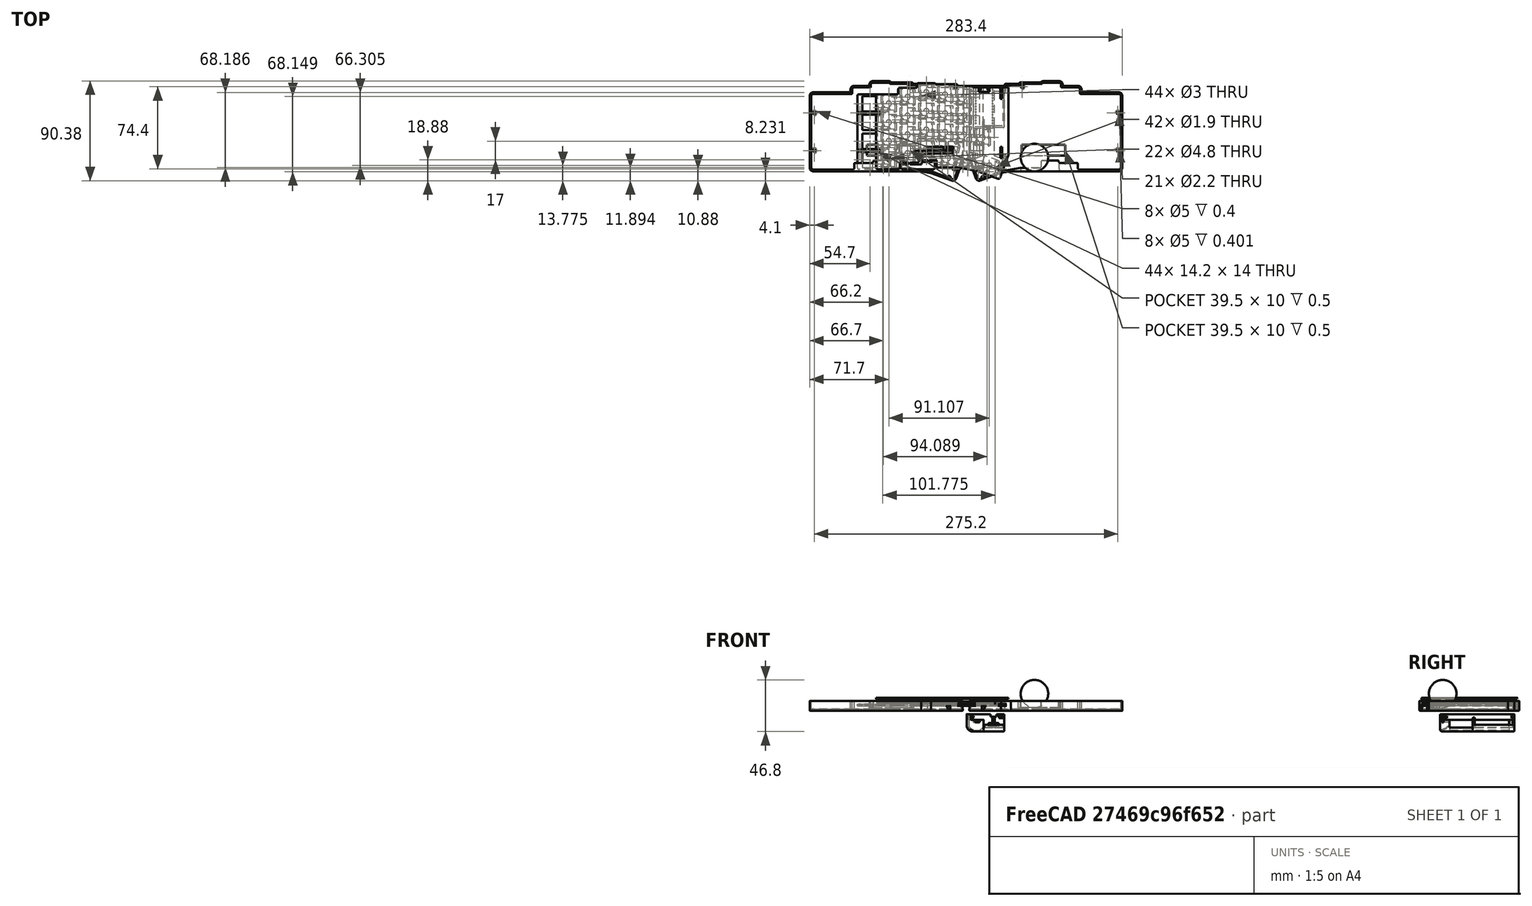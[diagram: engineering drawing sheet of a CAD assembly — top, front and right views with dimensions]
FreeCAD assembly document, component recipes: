
FREECAD ASSEMBLY — COMPONENT RECIPES ("simple-case-MS")

This assembly document has 5 components, labeled P0..P4 below (a component is one placed body or linked part). 4 of them carry a construction recipe — the FreeCAD feature program that regenerates the part from scratch, quoted from this document or its linked companion documents; the rest are supplied as boundary geometry only. No exploded tour is included for this assembly.
NOTE — document 2 of 3 of this assembly tour. The two overview renders and the header above are repeated from document 1; the component sections below continue where the previous document stopped.
COMPONENT P2 — recipe-attached ("case-key001", modeled in this document).
Construction recipe (the document's own serialized feature program — sketch geometry with constraints, then the solid features built on it; lengths are millimeters unless a unit is written):

FEATURE [Sketcher::SketchObject] Sketch020  label="top-plate"
  ArcFitTolerance = 1e-06
  ExternalTypes = [0]
  FullyConstrained = true
  MakeInternals = false
  Placement = pos=(0,0,6.6e-15) rot=(0,0,1;0rad)
  _ExternalGeoVersion = 0
  sketch-geometry (128):
    g0: ArcOfCircle CenterX=45.3 CenterY=2.4 CenterZ=0 NormalX=-1e-16 NormalY=0 NormalZ=1 AngleXU=1.5708 Radius=1.5 StartAngle=0 EndAngle=1.22777
    g1: LineSegment StartX=59.4 StartY=3.9 StartZ=0 EndX=45.3 EndY=3.9 EndZ=0
    g2: LineSegment StartX=43.8874 StartY=2.9045 StartZ=0 EndX=43.8874 EndY=2.8 EndZ=0
    g3: ArcOfCircle CenterX=59.4 CenterY=2.4 CenterZ=0 NormalX=-1e-16 NormalY=0 NormalZ=1 AngleXU=3.90995e-07 Radius=1.5 StartAngle=0 EndAngle=1.5708
    g4: LineSegment StartX=60.9 StartY=-0.4 StartZ=0 EndX=60.9 EndY=2.4 EndZ=0
    g5: LineSegment StartX=76.4 StartY=-0.4 StartZ=0 EndX=60.9 EndY=-0.4 EndZ=0
    g6: ArcOfCircle CenterX=76.4 CenterY=-1.9 CenterZ=0 NormalX=-1e-16 NormalY=0 NormalZ=1 AngleXU=3.90995e-07 Radius=1.5 StartAngle=0 EndAngle=1.5708
    g7: LineSegment StartX=77.9 StartY=-6.3 StartZ=0 EndX=77.9 EndY=-1.9 EndZ=0
    g8: LineSegment StartX=96.4 StartY=-6.3 StartZ=0 EndX=77.9 EndY=-6.3 EndZ=0
    g9: ArcOfCircle CenterX=96.4 CenterY=-7.8 CenterZ=0 NormalX=-1e-16 NormalY=0 NormalZ=1 AngleXU=3.90995e-07 Radius=1.5 StartAngle=0 EndAngle=1.5708
    g10: LineSegment StartX=97.9 StartY=-59.8 StartZ=0 EndX=97.9 EndY=-7.8 EndZ=0
    g11: LineSegment StartX=97.9 StartY=-72.8 StartZ=0 EndX=97.9 EndY=-59.8 EndZ=0
    g12: ArcOfCircle CenterX=96.4 CenterY=-72.8 CenterZ=0 NormalX=-1e-16 NormalY=0 NormalZ=1 AngleXU=-1.5708 Radius=1.5 StartAngle=0 EndAngle=1.5708
    g13: LineSegment StartX=78 StartY=-74.3 StartZ=0 EndX=96.4 EndY=-74.3 EndZ=0
    g14: ArcOfCircle CenterX=78 CenterY=-72.8 CenterZ=0 NormalX=-1e-16 NormalY=0 NormalZ=1 AngleXU=-3.14159 Radius=1.5 StartAngle=0 EndAngle=1.5708
    g15: LineSegment StartX=76.5 StartY=-68.4 StartZ=0 EndX=76.5 EndY=-72.8 EndZ=0
    g16: LineSegment StartX=60.7 StartY=-68.4 StartZ=0 EndX=76.5 EndY=-68.4 EndZ=0
    g17: ArcOfCircle CenterX=60.7 CenterY=-66.9 CenterZ=0 NormalX=-1e-16 NormalY=0 NormalZ=1 AngleXU=-3.14159 Radius=1.5 StartAngle=0 EndAngle=1.5708
    g18: LineSegment StartX=59.2 StartY=-66.1 StartZ=0 EndX=59.2 EndY=-66.9 EndZ=0
    g19: LineSegment StartX=43.1 StartY=-66.1 StartZ=0 EndX=59.2 EndY=-66.1 EndZ=0
    g20: LineSegment StartX=43.1 StartY=-71.2 StartZ=0 EndX=43.1 EndY=-66.1 EndZ=0
    g21: ArcOfCircle CenterX=41.6 CenterY=-71.2 CenterZ=0 NormalX=-1e-16 NormalY=0 NormalZ=1 AngleXU=-1.5708 Radius=1.5 StartAngle=0 EndAngle=1.5708
    g22: LineSegment StartX=41.4 StartY=-72.7 StartZ=0 EndX=41.6 EndY=-72.7 EndZ=0
    g23: LineSegment StartX=24.227 StartY=-72.7043 StartZ=0 EndX=41.4 EndY=-72.7 EndZ=0
    g24: LineSegment StartX=6.18739 StartY=-75.9853 StartZ=0 EndX=24.227 EndY=-72.7043 EndZ=0
    g25: LineSegment StartX=-12.4977 StartY=-82.7894 StartZ=0 EndX=6.18739 EndY=-75.9853 EndZ=0
    g26: ArcOfCircle CenterX=-13.0109 CenterY=-81.3798 CenterZ=0 NormalX=-1e-16 NormalY=0 NormalZ=1 AngleXU=-2.78723 Radius=1.50005 StartAngle=0 EndAngle=1.56562
    g27: LineSegment StartX=-20.3 StartY=-66 StartZ=0 EndX=-14.4178 EndY=-81.9004 EndZ=0
    g28: LineSegment StartX=-9.1 StartY=-61.9235 StartZ=0 EndX=-20.3 EndY=-66 EndZ=0
    g29: LineSegment StartX=-9.1 StartY=-61 StartZ=0 EndX=-9.1 EndY=-61.9235 EndZ=0
    g30: LineSegment StartX=-9.1 StartY=-36.9 StartZ=0 EndX=-9.1 EndY=-61 EndZ=0
    g31: LineSegment StartX=9.9 StartY=-36.9 StartZ=0 EndX=-9.1 EndY=-36.9 EndZ=0
    g32: LineSegment StartX=9.9 StartY=1.3 StartZ=0 EndX=9.9 EndY=-36.9 EndZ=0
    g33: LineSegment StartX=23.7 StartY=1.3 StartZ=0 EndX=9.9 EndY=1.3 EndZ=0
    g34: ArcOfCircle CenterX=25.2 CenterY=1.3 CenterZ=0 NormalX=-1e-16 NormalY=0 NormalZ=1 AngleXU=1.5708 Radius=1.5 StartAngle=0 EndAngle=1.5708
    g35: LineSegment StartX=43.8874 StartY=2.8 StartZ=0 EndX=25.2 EndY=2.8 EndZ=0
    g36: LineSegment StartX=93.5 StartY=-72.8 StartZ=0 EndX=79.3 EndY=-72.8 EndZ=0
    g37: LineSegment StartX=93.5 StartY=-58.8 StartZ=0 EndX=93.5 EndY=-72.8 EndZ=0
    g38: LineSegment StartX=79.3 StartY=-58.8 StartZ=0 EndX=93.5 EndY=-58.8 EndZ=0
    g39: LineSegment StartX=79.3 StartY=-72.8 StartZ=0 EndX=79.3 EndY=-58.8 EndZ=0
    g40: LineSegment StartX=76.5 StartY=-66.85 StartZ=0 EndX=62.3 EndY=-66.85 EndZ=0
    g41: LineSegment StartX=76.5 StartY=-52.85 StartZ=0 EndX=76.5 EndY=-66.85 EndZ=0
    g42: LineSegment StartX=62.3 StartY=-52.85 StartZ=0 EndX=76.5 EndY=-52.85 EndZ=0
    g43: LineSegment StartX=62.3 StartY=-66.85 StartZ=0 EndX=62.3 EndY=-52.85 EndZ=0
    g44: Circle CenterX=95.6 CenterY=-57.3 CenterZ=0 NormalX=-1e-16 NormalY=0 NormalZ=1 AngleXU=-1.5708 Radius=1.1
    g45: LineSegment StartX=93.5 StartY=-55.8 StartZ=0 EndX=79.3 EndY=-55.8 EndZ=0
    g46: LineSegment StartX=93.5 StartY=-41.8 StartZ=0 EndX=93.5 EndY=-55.8 EndZ=0
    g47: LineSegment StartX=79.3 StartY=-41.8 StartZ=0 EndX=93.5 EndY=-41.8 EndZ=0
    g48: LineSegment StartX=79.3 StartY=-55.8 StartZ=0 EndX=79.3 EndY=-41.8 EndZ=0
    g49: LineSegment StartX=76.5 StartY=-49.85 StartZ=0 EndX=62.3 EndY=-49.85 EndZ=0
    g50: LineSegment StartX=76.5 StartY=-35.85 StartZ=0 EndX=76.5 EndY=-49.85 EndZ=0
    g51: LineSegment StartX=62.3 StartY=-35.85 StartZ=0 EndX=76.5 EndY=-35.85 EndZ=0
    g52: LineSegment StartX=62.3 StartY=-49.85 StartZ=0 EndX=62.3 EndY=-35.85 EndZ=0
    g53: LineSegment StartX=59.5 StartY=-62.6 StartZ=0 EndX=45.3 EndY=-62.6 EndZ=0
    g54: LineSegment StartX=59.5 StartY=-48.6 StartZ=0 EndX=59.5 EndY=-62.6 EndZ=0
    g55: LineSegment StartX=45.3 StartY=-48.6 StartZ=0 EndX=59.5 EndY=-48.6 EndZ=0
    g56: LineSegment StartX=45.3 StartY=-62.6 StartZ=0 EndX=45.3 EndY=-48.6 EndZ=0
    g57: LineSegment StartX=39.95 StartY=-71.1 StartZ=0 EndX=25.75 EndY=-71.1 EndZ=0
    g58: LineSegment StartX=39.95 StartY=-57.1 StartZ=0 EndX=39.95 EndY=-71.1 EndZ=0
    g59: LineSegment StartX=25.75 StartY=-57.1 StartZ=0 EndX=39.95 EndY=-57.1 EndZ=0
    g60: LineSegment StartX=25.75 StartY=-71.1 StartZ=0 EndX=25.75 EndY=-57.1 EndZ=0
    g61: LineSegment StartX=21.8608 StartY=-71.3659 StartZ=0 EndX=7.87653 EndY=-73.8317 EndZ=0
    g62: LineSegment StartX=19.4297 StartY=-57.5786 StartZ=0 EndX=21.8608 EndY=-71.3659 EndZ=0
    g63: LineSegment StartX=5.44545 StartY=-60.0444 StartZ=0 EndX=19.4297 EndY=-57.5786 EndZ=0
    g64: LineSegment StartX=7.87653 StartY=-73.8317 StartZ=0 EndX=5.44545 EndY=-60.0444 EndZ=0
    g65: LineSegment StartX=4.35879 StartY=-75.0546 StartZ=0 EndX=-8.98485 EndY=-79.9113 EndZ=0
    g66: LineSegment StartX=-0.429495 StartY=-61.8989 StartZ=0 EndX=4.35879 EndY=-75.0546 EndZ=0
    g67: LineSegment StartX=-13.7731 StartY=-66.7556 StartZ=0 EndX=-0.429495 EndY=-61.8989 EndZ=0
    g68: LineSegment StartX=-8.98485 StartY=-79.9113 StartZ=0 EndX=-13.7731 EndY=-66.7556 EndZ=0
    g69: Circle CenterX=-14 CenterY=-73.8 CenterZ=0 NormalX=-1e-16 NormalY=0 NormalZ=1 AngleXU=-1.5708 Radius=1.1
    g70: LineSegment StartX=42.5 StartY=-47.725 StartZ=0 EndX=28.3 EndY=-47.725 EndZ=0
    g71: LineSegment StartX=42.5 StartY=-33.725 StartZ=0 EndX=42.5 EndY=-47.725 EndZ=0
    g72: LineSegment StartX=28.3 StartY=-33.725 StartZ=0 EndX=42.5 EndY=-33.725 EndZ=0
    g73: LineSegment StartX=28.3 StartY=-47.725 StartZ=0 EndX=28.3 EndY=-33.725 EndZ=0
    g74: LineSegment StartX=25.5 StartY=-49.85 StartZ=0 EndX=11.3 EndY=-49.85 EndZ=0
    g75: LineSegment StartX=25.5 StartY=-35.85 StartZ=0 EndX=25.5 EndY=-49.85 EndZ=0
    g76: LineSegment StartX=11.3 StartY=-35.85 StartZ=0 EndX=25.5 EndY=-35.85 EndZ=0
    g77: LineSegment StartX=11.3 StartY=-49.85 StartZ=0 EndX=11.3 EndY=-35.85 EndZ=0
    g78: LineSegment StartX=8.5 StartY=-52.4 StartZ=0 EndX=-5.7 EndY=-52.4 EndZ=0
    g79: LineSegment StartX=8.5 StartY=-38.4 StartZ=0 EndX=8.5 EndY=-52.4 EndZ=0
    g80: LineSegment StartX=-5.7 StartY=-38.4 StartZ=0 EndX=8.5 EndY=-38.4 EndZ=0
    g81: LineSegment StartX=-5.7 StartY=-52.4 StartZ=0 EndX=-5.7 EndY=-38.4 EndZ=0
    g82: LineSegment StartX=93.5 StartY=-38.8 StartZ=0 EndX=79.3 EndY=-38.8 EndZ=0
    g83: LineSegment StartX=93.5 StartY=-24.8 StartZ=0 EndX=93.5 EndY=-38.8 EndZ=0
    g84: LineSegment StartX=79.3 StartY=-24.8 StartZ=0 EndX=93.5 EndY=-24.8 EndZ=0
    g85: LineSegment StartX=79.3 StartY=-38.8 StartZ=0 EndX=79.3 EndY=-24.8 EndZ=0
    g86: Circle CenterX=95.6 CenterY=-23.3 CenterZ=0 NormalX=-1e-16 NormalY=0 NormalZ=1 AngleXU=-1.5708 Radius=1.1
    g87: LineSegment StartX=76.5 StartY=-32.85 StartZ=0 EndX=62.3 EndY=-32.85 EndZ=0
    g88: LineSegment StartX=76.5 StartY=-18.85 StartZ=0 EndX=76.5 EndY=-32.85 EndZ=0
    g89: LineSegment StartX=62.3 StartY=-18.85 StartZ=0 EndX=76.5 EndY=-18.85 EndZ=0
    g90: LineSegment StartX=62.3 StartY=-32.85 StartZ=0 EndX=62.3 EndY=-18.85 EndZ=0
    g91: LineSegment StartX=59.5 StartY=-45.6 StartZ=0 EndX=45.3 EndY=-45.6 EndZ=0
    g92: LineSegment StartX=59.5 StartY=-31.6 StartZ=0 EndX=59.5 EndY=-45.6 EndZ=0
    g93: LineSegment StartX=45.3 StartY=-31.6 StartZ=0 EndX=59.5 EndY=-31.6 EndZ=0
    g94: LineSegment StartX=45.3 StartY=-45.6 StartZ=0 EndX=45.3 EndY=-31.6 EndZ=0
    g95: LineSegment StartX=59.5 StartY=-28.6 StartZ=0 EndX=45.3 EndY=-28.6 EndZ=0
    g96: LineSegment StartX=59.5 StartY=-14.6 StartZ=0 EndX=59.5 EndY=-28.6 EndZ=0
    g97: LineSegment StartX=45.3 StartY=-14.6 StartZ=0 EndX=59.5 EndY=-14.6 EndZ=0
    g98: LineSegment StartX=45.3 StartY=-28.6 StartZ=0 EndX=45.3 EndY=-14.6 EndZ=0
    g99: LineSegment StartX=93.5 StartY=-21.8 StartZ=0 EndX=79.3 EndY=-21.8 EndZ=0
    g100: LineSegment StartX=93.5 StartY=-7.8 StartZ=0 EndX=93.5 EndY=-21.8 EndZ=0
    g101: LineSegment StartX=79.3 StartY=-7.8 StartZ=0 EndX=93.5 EndY=-7.8 EndZ=0
    g102: LineSegment StartX=79.3 StartY=-21.8 StartZ=0 EndX=79.3 EndY=-7.8 EndZ=0
    g103: LineSegment StartX=76.5 StartY=-15.85 StartZ=0 EndX=62.3 EndY=-15.85 EndZ=0
    g104: LineSegment StartX=76.5 StartY=-1.85 StartZ=0 EndX=76.5 EndY=-15.85 EndZ=0
    g105: LineSegment StartX=62.3 StartY=-1.85 StartZ=0 EndX=76.5 EndY=-1.85 EndZ=0
    g106: LineSegment StartX=62.3 StartY=-15.85 StartZ=0 EndX=62.3 EndY=-1.85 EndZ=0
    g107: LineSegment StartX=59.5 StartY=-11.6 StartZ=0 EndX=45.3 EndY=-11.6 EndZ=0
    g108: LineSegment StartX=59.5 StartY=2.4 StartZ=0 EndX=59.5 EndY=-11.6 EndZ=0
    g109: LineSegment StartX=45.3 StartY=2.4 StartZ=0 EndX=59.5 EndY=2.4 EndZ=0
    g110: LineSegment StartX=45.3 StartY=-11.6 StartZ=0 EndX=45.3 EndY=2.4 EndZ=0
    g111: LineSegment StartX=42.5 StartY=-30.725 StartZ=0 EndX=28.3 EndY=-30.725 EndZ=0
    g112: LineSegment StartX=42.5 StartY=-16.725 StartZ=0 EndX=42.5 EndY=-30.725 EndZ=0
    g113: LineSegment StartX=28.3 StartY=-16.725 StartZ=0 EndX=42.5 EndY=-16.725 EndZ=0
    g114: LineSegment StartX=28.3 StartY=-30.725 StartZ=0 EndX=28.3 EndY=-16.725 EndZ=0
    g115: LineSegment StartX=25.5 StartY=-32.85 StartZ=0 EndX=11.3 EndY=-32.85 EndZ=0
    g116: LineSegment StartX=25.5 StartY=-18.85 StartZ=0 EndX=25.5 EndY=-32.85 EndZ=0
    g117: LineSegment StartX=11.3 StartY=-18.85 StartZ=0 EndX=25.5 EndY=-18.85 EndZ=0
    g118: LineSegment StartX=11.3 StartY=-32.85 StartZ=0 EndX=11.3 EndY=-18.85 EndZ=0
    g119: LineSegment StartX=25.5 StartY=-15.85 StartZ=0 EndX=11.3 EndY=-15.85 EndZ=0
    g120: LineSegment StartX=25.5 StartY=-1.85 StartZ=0 EndX=25.5 EndY=-15.85 EndZ=0
    g121: LineSegment StartX=11.3 StartY=-1.85 StartZ=0 EndX=25.5 EndY=-1.85 EndZ=0
    g122: LineSegment StartX=11.3 StartY=-15.85 StartZ=0 EndX=11.3 EndY=-1.85 EndZ=0
    g123: LineSegment StartX=42.5 StartY=-13.725 StartZ=0 EndX=28.3 EndY=-13.725 EndZ=0
    g124: LineSegment StartX=42.5 StartY=0.275 StartZ=0 EndX=42.5 EndY=-13.725 EndZ=0
    g125: LineSegment StartX=28.3 StartY=0.275 StartZ=0 EndX=42.5 EndY=0.275 EndZ=0
    g126: LineSegment StartX=28.3 StartY=-13.725 StartZ=0 EndX=28.3 EndY=0.275 EndZ=0
    g127: Circle CenterX=25.9 CenterY=0.6 CenterZ=0 NormalX=-1e-16 NormalY=0 NormalZ=1 AngleXU=-1.5708 Radius=1.1
  constraints (252):
    c: Block(g0)
    c: Block(g1)
    c: Block(g2)
    c: Block(g3)
    c: Block(g4)
    c: Block(g5)
    c: Block(g6)
    c: Block(g7)
    c: Block(g8)
    c: Block(g9)
    c: Block(g10)
    c: Block(g11)
    c: Block(g12)
    c: Block(g13)
    c: Block(g14)
    c: Block(g15)
    c: Block(g16)
    c: Block(g17)
    c: Block(g18)
    c: Block(g19)
    c: Block(g20)
    c: Block(g21)
    c: Block(g22)
    c: Block(g23)
    c: Block(g24)
    c: Block(g25)
    c: Block(g26)
    c: Block(g27)
    c: Block(g28)
    c: Block(g29)
    c: Block(g30)
    c: Block(g31)
    c: Block(g32)
    c: Block(g33)
    c: Block(g34)
    c: Block(g35)
    c: Block(g36)
    c: Block(g37)
    c: Block(g38)
    c: Block(g39)
    c: Block(g40)
    c: Block(g41)
    c: Block(g42)
    c: Block(g43)
    c: Block(g44)
    c: Block(g45)
    c: Block(g46)
    c: Block(g47)
    c: Block(g48)
    c: Block(g49)
    c: Block(g50)
    c: Block(g51)
    c: Block(g52)
    c: Block(g53)
    c: Block(g54)
    c: Block(g55)
    c: Block(g56)
    c: Block(g57)
    c: Block(g58)
    c: Block(g59)
    c: Block(g60)
    c: Block(g61)
    c: Block(g62)
    c: Block(g63)
    c: Block(g64)
    c: Block(g65)
    c: Block(g66)
    c: Block(g67)
    c: Block(g68)
    c: Block(g69)
    c: Block(g70)
    c: Block(g71)
    c: Block(g72)
    c: Block(g73)
    c: Block(g74)
    c: Block(g75)
    c: Block(g76)
    c: Block(g77)
    c: Block(g78)
    c: Block(g79)
    c: Block(g80)
    c: Block(g81)
    c: Block(g82)
    c: Block(g83)
    c: Block(g84)
    c: Block(g85)
    c: Block(g86)
    c: Block(g87)
    c: Block(g88)
    c: Block(g89)
    c: Block(g90)
    c: Block(g91)
    c: Block(g92)
    c: Block(g93)
    c: Block(g94)
    c: Block(g95)
    c: Block(g96)
    c: Block(g97)
    c: Block(g98)
    c: Block(g99)
    c: Block(g100)
    c: Block(g101)
    c: Block(g102)
    c: Block(g103)
    c: Block(g104)
    c: Block(g105)
    c: Block(g106)
    c: Block(g107)
    c: Block(g108)
    c: Block(g109)
    c: Block(g110)
    c: Block(g111)
    c: Block(g112)
    c: Block(g113)
    c: Block(g114)
    c: Block(g115)
    c: Block(g116)
    c: Block(g117)
    c: Block(g118)
    c: Block(g119)
    c: Block(g120)
    c: Block(g121)
    c: Block(g122)
    c: Block(g123)
    c: Block(g124)
    c: Block(g125)
    c: Block(g126)
    c: Block(g127)
    c: Coincident(g27,g28)
    c: Coincident(g26,g27)
    c: Coincident(g67,g68)
    c: Coincident(g25,g26)
    c: Coincident(g28,g29)
    c: Coincident(g29,g30)
    c: Coincident(g30,g31)
    c: Coincident(g65,g68)
    c: Coincident(g78,g81)
    c: Coincident(g80,g81)
    c: Coincident(g66,g67)
    c: Coincident(g65,g66)
    c: Coincident(g63,g64)
    c: Coincident(g24,g25)
    c: Coincident(g61,g64)
    c: Coincident(g78,g79)
    c: Coincident(g79,g80)
    c: Coincident(g31,g32)
    c: Coincident(g32,g33)
    c: Coincident(g74,g77)
    c: Coincident(g76,g77)
    c: Coincident(g115,g118)
    c: Coincident(g117,g118)
    c: Coincident(g119,g122)
    c: Coincident(g121,g122)
    c: Coincident(g62,g63)
    c: Coincident(g61,g62)
    c: Coincident(g33,g34)
    c: Coincident(g23,g24)
    c: Coincident(g34,g35)
    c: Coincident(g74,g75)
    c: Coincident(g75,g76)
    c: Coincident(g115,g116)
    c: Coincident(g116,g117)
    c: Coincident(g119,g120)
    c: Coincident(g120,g121)
    c: Coincident(g57,g60)
    c: Coincident(g59,g60)
    c: Coincident(g70,g73)
    c: Coincident(g72,g73)
    c: Coincident(g111,g114)
    c: Coincident(g113,g114)
    c: Coincident(g123,g126)
    c: Coincident(g125,g126)
    c: Coincident(g57,g58)
    c: Coincident(g58,g59)
    c: Coincident(g22,g23)
    c: Coincident(g21,g22)
    c: Coincident(g70,g71)
    c: Coincident(g71,g72)
    c: Coincident(g111,g112)
    c: Coincident(g112,g113)
    c: Coincident(g123,g124)
    c: Coincident(g124,g125)
    c: Coincident(g20,g21)
    c: Coincident(g19,g20)
    c: Coincident(g2,g35)
    c: Coincident(g0,g2)
    c: Coincident(g53,g56)
    c: Coincident(g55,g56)
    c: Coincident(g91,g94)
    c: Coincident(g93,g94)
    c: Coincident(g95,g98)
    c: Coincident(g97,g98)
    c: Coincident(g107,g110)
    c: Coincident(g109,g110)
    c: Coincident(g0,g1)
    c: Coincident(g17,g18)
    c: Coincident(g18,g19)
    c: Coincident(g1,g3)
    c: Coincident(g53,g54)
    c: Coincident(g54,g55)
    c: Coincident(g91,g92)
    c: Coincident(g92,g93)
    c: Coincident(g95,g96)
    c: Coincident(g96,g97)
    c: Coincident(g107,g108)
    c: Coincident(g108,g109)
    c: Coincident(g16,g17)
    c: Coincident(g4,g5)
    c: Coincident(g3,g4)
    c: Coincident(g40,g43)
    c: Coincident(g42,g43)
    c: Coincident(g49,g52)
    c: Coincident(g51,g52)
    c: Coincident(g87,g90)
    c: Coincident(g89,g90)
    c: Coincident(g103,g106)
    c: Coincident(g105,g106)
    c: Coincident(g5,g6)
    c: Coincident(g14,g15)
    c: Coincident(g15,g16)
    c: Coincident(g40,g41)
    c: Coincident(g41,g42)
    c: Coincident(g49,g50)
    c: Coincident(g50,g51)
    c: Coincident(g87,g88)
    c: Coincident(g88,g89)
    c: Coincident(g103,g104)
    c: Coincident(g104,g105)
    c: Coincident(g7,g8)
    c: Coincident(g6,g7)
    c: Coincident(g13,g14)
    c: Coincident(g36,g39)
    c: Coincident(g38,g39)
    c: Coincident(g45,g48)
    c: Coincident(g47,g48)
    c: Coincident(g82,g85)
    c: Coincident(g84,g85)
    c: Coincident(g99,g102)
    c: Coincident(g101,g102)
    c: Coincident(g36,g37)
    c: Coincident(g37,g38)
    c: Coincident(g45,g46)
    c: Coincident(g46,g47)
    c: Coincident(g82,g83)
    c: Coincident(g83,g84)
    c: Coincident(g99,g100)
    c: Coincident(g100,g101)
    c: Coincident(g12,g13)
    c: Coincident(g8,g9)
    c: Coincident(g11,g12)
    c: Coincident(g10,g11)
    c: Coincident(g9,g10)
FEATURE [Sketcher::SketchObject] Sketch021
  ArcFitTolerance = 1e-06
  AttachmentOffset = pos=(0,0,-5.1) rot=(0,0,1;0rad)
  AttachmentSupport = -> [XY_Plane004]
  ExternalTypes = [0]
  FullyConstrained = false
  MakeInternals = false
  MapMode = 5
  Placement = pos=(0,0,-5.1) rot=(0,0,1;0rad)
  _ExternalGeoVersion = 0
  sketch-geometry (65):
    g0: ArcOfCircle [constr] CenterX=45.3 CenterY=2.4 CenterZ=0 NormalX=-1e-16 NormalY=0 NormalZ=1 AngleXU=1.5708 Radius=1.5 StartAngle=0 EndAngle=1.22777
    g1: LineSegment [constr] StartX=59.4 StartY=3.9 StartZ=0 EndX=45.3 EndY=3.9 EndZ=0
    g2: LineSegment [constr] StartX=43.8874 StartY=2.9045 StartZ=0 EndX=43.8874 EndY=2.8 EndZ=0
    g3: ArcOfCircle [constr] CenterX=59.4 CenterY=2.4 CenterZ=0 NormalX=-1e-16 NormalY=0 NormalZ=1 AngleXU=3.90995e-07 Radius=1.5 StartAngle=0 EndAngle=1.5708
    g4: LineSegment [constr] StartX=60.9 StartY=-0.4 StartZ=0 EndX=60.9 EndY=2.4 EndZ=0
    g5: LineSegment [constr] StartX=76.4 StartY=-0.4 StartZ=0 EndX=60.9 EndY=-0.4 EndZ=0
    g6: ArcOfCircle [constr] CenterX=76.4 CenterY=-1.9 CenterZ=0 NormalX=-1e-16 NormalY=0 NormalZ=1 AngleXU=3.90995e-07 Radius=1.5 StartAngle=0 EndAngle=1.5708
    g7: LineSegment [constr] StartX=77.9 StartY=-6.3 StartZ=0 EndX=77.9 EndY=-1.9 EndZ=0
    g8: LineSegment [constr] StartX=96.4 StartY=-6.3 StartZ=0 EndX=77.9 EndY=-6.3 EndZ=0
    g9: ArcOfCircle [constr] CenterX=96.4 CenterY=-7.8 CenterZ=0 NormalX=-1e-16 NormalY=0 NormalZ=1 AngleXU=3.90995e-07 Radius=1.5 StartAngle=0 EndAngle=1.5708
    g10: LineSegment [constr] StartX=97.9 StartY=-59.8 StartZ=0 EndX=97.9 EndY=-7.8 EndZ=0
    g11: LineSegment [constr] StartX=97.9 StartY=-72.8 StartZ=0 EndX=97.9 EndY=-59.8 EndZ=0
    g12: ArcOfCircle [constr] CenterX=96.4 CenterY=-72.8 CenterZ=0 NormalX=-1e-16 NormalY=0 NormalZ=1 AngleXU=-1.5708 Radius=1.5 StartAngle=0 EndAngle=1.5708
    g13: LineSegment [constr] StartX=78 StartY=-74.3 StartZ=0 EndX=96.4 EndY=-74.3 EndZ=0
    g14: LineSegment [constr] StartX=6.18739 StartY=-75.9853 StartZ=0 EndX=15.4535 EndY=-74.3 EndZ=0
    g15: LineSegment [constr] StartX=-12.4977 StartY=-82.7894 StartZ=0 EndX=6.18739 EndY=-75.9853 EndZ=0
    g16: ArcOfCircle [constr] CenterX=-13.0109 CenterY=-81.3798 CenterZ=0 NormalX=-1e-16 NormalY=0 NormalZ=1 AngleXU=-2.78723 Radius=1.50005 StartAngle=0 EndAngle=1.56562
    g17: LineSegment [constr] StartX=-20.3 StartY=-66 StartZ=0 EndX=-14.4178 EndY=-81.9004 EndZ=0
    g18: LineSegment [constr] StartX=-9.1 StartY=-61.9235 StartZ=0 EndX=-20.3 EndY=-66 EndZ=0
    g19: LineSegment [constr] StartX=-9.1 StartY=-61 StartZ=0 EndX=-9.1 EndY=-61.9235 EndZ=0
    g20: LineSegment [constr] StartX=-9.1 StartY=-36.9 StartZ=0 EndX=-9.1 EndY=-61 EndZ=0
    g21: LineSegment [constr] StartX=9.9 StartY=-36.9 StartZ=0 EndX=-9.1 EndY=-36.9 EndZ=0
    g22: LineSegment [constr] StartX=9.9 StartY=1.3 StartZ=0 EndX=9.9 EndY=-36.9 EndZ=0
    g23: LineSegment [constr] StartX=23.7 StartY=1.3 StartZ=0 EndX=9.9 EndY=1.3 EndZ=0
    g24: ArcOfCircle [constr] CenterX=25.2 CenterY=1.3 CenterZ=0 NormalX=-1e-16 NormalY=0 NormalZ=1 AngleXU=1.5708 Radius=1.5 StartAngle=0 EndAngle=1.5708
    g25: LineSegment [constr] StartX=43.8874 StartY=2.8 StartZ=0 EndX=25.2 EndY=2.8 EndZ=0
    g26: LineSegment [constr] StartX=78 StartY=-74.3 StartZ=0 EndX=15.4535 EndY=-74.3 EndZ=0
    g27: LineSegment StartX=78 StartY=-76.1 StartZ=0 EndX=15.6159 EndY=-76.1 EndZ=0
    g28: LineSegment StartX=6.65976 StartY=-77.7289 StartZ=0 EndX=15.6159 EndY=-76.1 EndZ=0
    g29: LineSegment StartX=-11.8818 StartY=-84.4807 StartZ=0 EndX=6.65976 EndY=-77.7289 EndZ=0
    g30: ArcOfCircle CenterX=-13.0109 CenterY=-81.3798 CenterZ=0 NormalX=0 NormalY=0 NormalZ=1 AngleXU=-2.78723 Radius=3.30007 StartAngle=6.28318 EndAngle=7.84881
    g31: LineSegment StartX=-21.9882 StartY=-66.6245 StartZ=0 EndX=-16.106 EndY=-82.5249 EndZ=0
    g32: LineSegment [constr] StartX=-10.9 StartY=-60.6632 StartZ=0 EndX=-20.9156 EndY=-64.3086 EndZ=0
    g33: LineSegment [constr] StartX=-10.9 StartY=-36.9 StartZ=0 EndX=-10.9 EndY=-60.6632 EndZ=0
    g34: ArcOfCircle [constr] CenterX=-9.1 CenterY=-36.9 CenterZ=0 NormalX=0 NormalY=0 NormalZ=1 AngleXU=0 Radius=1.8 StartAngle=1.5708 EndAngle=3.14159
    g35: LineSegment [constr] StartX=8.1 StartY=-35.1 StartZ=0 EndX=-9.1 EndY=-35.1 EndZ=0
    g36: LineSegment [constr] StartX=8.1 StartY=1.3 StartZ=0 EndX=8.1 EndY=-35.1 EndZ=0
    g37: ArcOfCircle [constr] CenterX=9.9 CenterY=1.3 CenterZ=0 NormalX=0 NormalY=0 NormalZ=1 AngleXU=0 Radius=1.8 StartAngle=1.5708 EndAngle=3.14159
    g38: LineSegment [constr] StartX=22.4341 StartY=3.1 StartZ=0 EndX=9.9 EndY=3.1 EndZ=0
    g39: ArcOfCircle CenterX=25.2 CenterY=1.3 CenterZ=0 NormalX=0 NormalY=0 NormalZ=1 AngleXU=1.5708 Radius=3.3 StartAngle=0 EndAngle=0.993864
    g40: LineSegment StartX=42.8403 StartY=4.6 StartZ=0 EndX=25.2 EndY=4.6 EndZ=0
    g41: ArcOfCircle CenterX=45.3 CenterY=2.4 CenterZ=0 NormalX=0 NormalY=0 NormalZ=1 AngleXU=1.5708 Radius=3.3 StartAngle=0 EndAngle=0.841069
    g42: LineSegment StartX=59.4 StartY=5.7 StartZ=0 EndX=45.3 EndY=5.7 EndZ=0
    g43: ArcOfCircle CenterX=59.4 CenterY=2.4 CenterZ=0 NormalX=0 NormalY=0 NormalZ=1 AngleXU=3.90995e-07 Radius=3.3 StartAngle=-1.8e-15 EndAngle=1.5708
    g44: LineSegment StartX=62.7 StartY=1.4 StartZ=0 EndX=62.7 EndY=2.4 EndZ=0
    g45: LineSegment StartX=76.4 StartY=1.4 StartZ=0 EndX=62.7 EndY=1.4 EndZ=0
    g46: ArcOfCircle CenterX=76.4 CenterY=-1.9 CenterZ=0 NormalX=0 NormalY=0 NormalZ=1 AngleXU=3.90995e-07 Radius=3.3 StartAngle=-1.8e-15 EndAngle=1.5708
    g47: LineSegment StartX=79.7 StartY=-4.5 StartZ=0 EndX=79.7 EndY=-1.9 EndZ=0
    g48: LineSegment StartX=113.4 StartY=-4.5 StartZ=0 EndX=79.7 EndY=-4.5 EndZ=0
    g49: ArcOfCircle CenterX=113.4 CenterY=-7.8 CenterZ=0 NormalX=0 NormalY=0 NormalZ=1 AngleXU=3.90995e-07 Radius=3.3 StartAngle=6.28318 EndAngle=7.85398
    g50: LineSegment StartX=116.7 StartY=-59.8 StartZ=0 EndX=116.7 EndY=-7.8 EndZ=0
    g51: LineSegment StartX=116.7 StartY=-72.8 StartZ=0 EndX=116.7 EndY=-59.8 EndZ=0
    g52: ArcOfCircle CenterX=113.4 CenterY=-72.8 CenterZ=0 NormalX=0 NormalY=0 NormalZ=1 AngleXU=-1.5708 Radius=3.3 StartAngle=6.28318 EndAngle=7.85398
    g53: LineSegment StartX=78 StartY=-76.1 StartZ=0 EndX=113.4 EndY=-76.1 EndZ=0
    g54: LineSegment [constr] StartX=8.1 StartY=1.3 StartZ=0 EndX=8.1 EndY=0 EndZ=0
    g55: LineSegment StartX=8.1 StartY=0 StartZ=0 EndX=-22.1 EndY=0 EndZ=0
    g56: LineSegment StartX=-22.1 StartY=0 StartZ=0 EndX=-22.1 EndY=-61.0545 EndZ=0
    g57: LineSegment StartX=-22.1 StartY=-61.0545 StartZ=0 EndX=-20.3 EndY=-66 EndZ=0
    g58: LineSegment StartX=-20.3 StartY=-66 StartZ=0 EndX=-21.9882 EndY=-66.6245 EndZ=0
    g59: LineSegment StartX=22.4341 StartY=3.1 StartZ=0 EndX=8.1 EndY=3.1 EndZ=0
    g60: LineSegment StartX=8.1 StartY=3.1 StartZ=0 EndX=8.1 EndY=0 EndZ=0
    g61: LineSegment [constr] StartX=113.4 StartY=-4.5 StartZ=0 EndX=113.4 EndY=-7.8 EndZ=0
    g62: LineSegment [constr] StartX=113.4 StartY=-7.8 StartZ=0 EndX=116.7 EndY=-7.8 EndZ=0
    g63: LineSegment [constr] StartX=113.4 StartY=-72.8 StartZ=0 EndX=113.4 EndY=-76.1 EndZ=0
    g64: LineSegment [constr] StartX=113.4 StartY=-72.8 StartZ=0 EndX=116.7 EndY=-72.8 EndZ=0
  constraints (124):
    c: Block(g0)
    c: Block(g1)
    c: Block(g2)
    c: Block(g3)
    c: Block(g4)
    c: Block(g5)
    c: Block(g6)
    c: Block(g7)
    c: Block(g8)
    c: Block(g9)
    c: Block(g10)
    c: Block(g11)
    c: Block(g12)
    c: Block(g13)
    c: Block(g14)
    c: Block(g15)
    c: Block(g16)
    c: Block(g17)
    c: Block(g18)
    c: Block(g19)
    c: Block(g20)
    c: Block(g21)
    c: Block(g22)
    c: Block(g23)
    c: Block(g24)
    c: Block(g25)
    c: Coincident(g17,g18)
    c: Coincident(g16,g17)
    c: Coincident(g15,g16)
    c: Coincident(g18,g19)
    c: Coincident(g19,g20)
    c: Coincident(g20,g21)
    c: Coincident(g14,g15)
    c: Coincident(g21,g22)
    c: Coincident(g22,g23)
    c: Coincident(g23,g24)
    c: Coincident(g24,g25)
    c: Coincident(g2,g25)
    c: Coincident(g0,g2)
    c: Coincident(g0,g1)
    c: Coincident(g1,g3)
    c: Coincident(g4,g5)
    c: Coincident(g3,g4)
    c: Coincident(g5,g6)
    c: Coincident(g7,g8)
    c: Coincident(g6,g7)
    c: Coincident(g12,g13)
    c: Coincident(g8,g9)
    c: Coincident(g11,g12)
    c: Coincident(g10,g11)
    c: Coincident(g9,g10)
    c: Coincident(g26,g13)
    c: Horizontal(g26)
    c: Coincident(g14,g26)
    c: Coincident(g27,g28)
    c: Coincident(g27,g53)
    c: Coincident(g28,g29)
    c: Coincident(g32,g33)
    c: Tangent(g33,g34) = -1.5708
    c: Tangent(g34,g35) = -1.5708
    c: Coincident(g35,g36)
    c: Tangent(g36,g37) = -1.5708
    c: Tangent(g37,g38) = -1.5708
    c: Coincident(g38,g39)
    c: Coincident(g40,g41)
    c: Coincident(g44,g45)
    c: Coincident(g47,g48)
    c: Coincident(g50,g51)
    c: Coincident(g54,g36)
    c: PointOnObject(g54,g-1)
    c: Vertical(g54)
    c: Coincident(g55,g54)
    c: PointOnObject(g55,g-1)
    c: Coincident(g56,g55)
    c: Vertical(g56)
    c: DistanceX(g55,g-1) = 22.1
    c: Coincident(g57,g56)
    c: Coincident(g57,g17)
    c: Angle(g18,g57) = 1.5708
    c: Coincident(g58,g17)
    c: Coincident(g58,g31)
    c: Coincident(g30,g31)
    c: Coincident(g29,g30)
    c: Coincident(g39,g40)
    c: Coincident(g41,g42)
    c: Coincident(g42,g43)
    c: Coincident(g43,g44)
    c: Coincident(g45,g46)
    c: Coincident(g46,g47)
    c: Coincident(g52,g53)
    c: Coincident(g48,g49)
    c: Coincident(g51,g52)
    c: Coincident(g49,g50)
    c: Block(g38)
    c: Block(g36)
    c: Coincident(g59,g38)
    c: Horizontal(g59)
    c: Tangent(g59,g37)
    c: Coincident(g60,g59)
    c: Coincident(g60,g54)
    c: Vertical(g60)
    c: Block(g47)
    c: Block(g27)
    c: DistanceY(g48,g-1) = 4.5
    c: DistanceY(g52,g-1) = 76.1
    c: Horizontal(g53)
    c: Horizontal(g48)
    c: Radius(g49) = 3.3
    c: Radius(g52) = 3.3
    c: DistanceX(g-1,g49) = 116.7
    c: Vertical(g50)
    c: Vertical(g51)
    c: Coincident(g61,g48)
    c: Coincident(g61,g49)
    c: Vertical(g61)
    c: Coincident(g62,g49)
    c: Coincident(g62,g49)
    c: Horizontal(g62)
    c: Coincident(g63,g52)
    c: Coincident(g63,g52)
    c: Vertical(g63)
    c: Coincident(g64,g52)
    c: Coincident(g64,g51)
    c: Horizontal(g64)
FEATURE [PartDesign::Pad] Pad010
  Direction = (0,0,1)
  Length = 1.5
  Length2 = 7.3
  Profile = -> Sketch021
  ReferenceAxis = -> Sketch021 [N_Axis]
  Refine = true
  Reversed = true
  SideType = 1
  Suppressed = false
  Type = 0
  Type2 = 0
FEATURE [Sketcher::SketchObject] Sketch022  label="bottom-plate"
  ArcFitTolerance = 1e-06
  ExternalTypes = [0]
  FullyConstrained = true
  MakeInternals = false
  Placement = pos=(0,0,6.6e-15) rot=(0,0,1;0rad)
  _ExternalGeoVersion = 0
  sketch-geometry (74):
    g0: ArcOfCircle CenterX=45.3 CenterY=2.4 CenterZ=0 NormalX=-1e-16 NormalY=0 NormalZ=1 AngleXU=1.5708 Radius=1.5 StartAngle=0 EndAngle=1.22777
    g1: LineSegment StartX=59.4 StartY=3.9 StartZ=0 EndX=45.3 EndY=3.9 EndZ=0
    g2: LineSegment StartX=43.8874 StartY=2.9045 StartZ=0 EndX=43.8874 EndY=2.8 EndZ=0
    g3: ArcOfCircle CenterX=59.4 CenterY=2.4 CenterZ=0 NormalX=-1e-16 NormalY=0 NormalZ=1 AngleXU=3.90995e-07 Radius=1.5 StartAngle=0 EndAngle=1.5708
    g4: LineSegment StartX=60.9 StartY=-0.4 StartZ=0 EndX=60.9 EndY=2.4 EndZ=0
    g5: LineSegment StartX=76.4 StartY=-0.4 StartZ=0 EndX=60.9 EndY=-0.4 EndZ=0
    g6: ArcOfCircle CenterX=76.4 CenterY=-1.9 CenterZ=0 NormalX=-1e-16 NormalY=0 NormalZ=1 AngleXU=3.90995e-07 Radius=1.5 StartAngle=0 EndAngle=1.5708
    g7: LineSegment StartX=77.9 StartY=-6.3 StartZ=0 EndX=77.9 EndY=-1.9 EndZ=0
    g8: LineSegment StartX=96.4 StartY=-6.3 StartZ=0 EndX=77.9 EndY=-6.3 EndZ=0
    g9: ArcOfCircle CenterX=96.4 CenterY=-7.8 CenterZ=0 NormalX=-1e-16 NormalY=0 NormalZ=1 AngleXU=3.90995e-07 Radius=1.5 StartAngle=0 EndAngle=1.5708
    g10: LineSegment StartX=97.9 StartY=-59.8 StartZ=0 EndX=97.9 EndY=-7.8 EndZ=0
    g11: LineSegment StartX=97.9 StartY=-72.8 StartZ=0 EndX=97.9 EndY=-59.8 EndZ=0
    g12: ArcOfCircle CenterX=96.4 CenterY=-72.8 CenterZ=0 NormalX=-1e-16 NormalY=0 NormalZ=1 AngleXU=-1.5708 Radius=1.5 StartAngle=0 EndAngle=1.5708
    g13: LineSegment StartX=78 StartY=-74.3 StartZ=0 EndX=96.4 EndY=-74.3 EndZ=0
    g14: ArcOfCircle CenterX=78 CenterY=-72.8 CenterZ=0 NormalX=-1e-16 NormalY=0 NormalZ=1 AngleXU=-3.14159 Radius=1.5 StartAngle=0 EndAngle=1.5708
    g15: LineSegment StartX=76.5 StartY=-68.4 StartZ=0 EndX=76.5 EndY=-72.8 EndZ=0
    g16: LineSegment StartX=68.6 StartY=-68.4 StartZ=0 EndX=76.5 EndY=-68.4 EndZ=0
    g17: LineSegment StartX=68.6 StartY=-69.9 StartZ=0 EndX=68.6 EndY=-68.4 EndZ=0
    g18: LineSegment StartX=75 StartY=-69.9 StartZ=0 EndX=68.6 EndY=-69.9 EndZ=0
    g19: LineSegment StartX=75 StartY=-72.8 StartZ=0 EndX=75 EndY=-69.9 EndZ=0
    g20: ArcOfCircle CenterX=73.5 CenterY=-72.8 CenterZ=0 NormalX=-1e-16 NormalY=0 NormalZ=1 AngleXU=-1.5708 Radius=1.5 StartAngle=0 EndAngle=1.5708
    g21: LineSegment StartX=46.1 StartY=-74.3 StartZ=0 EndX=73.5 EndY=-74.3 EndZ=0
    g22: ArcOfCircle CenterX=46.1 CenterY=-72.8 CenterZ=0 NormalX=-1e-16 NormalY=0 NormalZ=1 AngleXU=-3.14159 Radius=1.5 StartAngle=0 EndAngle=1.5708
    g23: LineSegment StartX=44.6 StartY=-67.6 StartZ=0 EndX=44.6 EndY=-72.8 EndZ=0
    g24: LineSegment StartX=49.65 StartY=-67.6 StartZ=0 EndX=44.6 EndY=-67.6 EndZ=0
    g25: LineSegment StartX=49.65 StartY=-66.1 StartZ=0 EndX=49.65 EndY=-67.6 EndZ=0
    g26: LineSegment StartX=43.1 StartY=-66.1 StartZ=0 EndX=49.65 EndY=-66.1 EndZ=0
    g27: LineSegment StartX=43.1 StartY=-71.2 StartZ=0 EndX=43.1 EndY=-66.1 EndZ=0
    g28: ArcOfCircle CenterX=41.6 CenterY=-71.2 CenterZ=0 NormalX=-1e-16 NormalY=0 NormalZ=1 AngleXU=-1.5708 Radius=1.5 StartAngle=0 EndAngle=1.5708
    g29: LineSegment StartX=41.4 StartY=-72.7 StartZ=0 EndX=41.6 EndY=-72.7 EndZ=0
    g30: LineSegment StartX=24.227 StartY=-72.7043 StartZ=0 EndX=41.4 EndY=-72.7 EndZ=0
    g31: LineSegment StartX=6.18739 StartY=-75.9853 StartZ=0 EndX=24.227 EndY=-72.7043 EndZ=0
    g32: LineSegment StartX=-12.4977 StartY=-82.7894 StartZ=0 EndX=6.18739 EndY=-75.9853 EndZ=0
    g33: ArcOfCircle CenterX=-13.011 CenterY=-81.3799 CenterZ=0 NormalX=-1e-16 NormalY=0 NormalZ=1 AngleXU=-2.78726 Radius=1.5 StartAngle=0 EndAngle=1.56568
    g34: LineSegment StartX=-22.1 StartY=-61.1344 StartZ=0 EndX=-14.4178 EndY=-81.9004 EndZ=0
    g35: LineSegment StartX=-22.1 StartY=0 StartZ=0 EndX=-22.1 EndY=-61.1344 EndZ=0
    g36: LineSegment StartX=-16.4 StartY=0 StartZ=0 EndX=-22.1 EndY=0 EndZ=0
    g37: LineSegment StartX=-16.4 StartY=-10.5 StartZ=0 EndX=-16.4 EndY=0 EndZ=0
    g38: LineSegment StartX=-14.8 StartY=-10.5 StartZ=0 EndX=-16.4 EndY=-10.5 EndZ=0
    g39: LineSegment StartX=-14.8 StartY=0 StartZ=0 EndX=-14.8 EndY=-10.5 EndZ=0
    g40: LineSegment StartX=-5 StartY=0 StartZ=0 EndX=-14.8 EndY=0 EndZ=0
    g41: LineSegment StartX=-5 StartY=-4 StartZ=0 EndX=-5 EndY=0 EndZ=0
    g42: LineSegment StartX=5 StartY=-4 StartZ=0 EndX=-5 EndY=-4 EndZ=0
    g43: LineSegment StartX=5 StartY=0 StartZ=0 EndX=5 EndY=-4 EndZ=0
    g44: LineSegment StartX=9.9 StartY=0 StartZ=0 EndX=5 EndY=0 EndZ=0
    g45: LineSegment StartX=9.9 StartY=1.3 StartZ=0 EndX=9.9 EndY=0 EndZ=0
    g46: LineSegment StartX=23.7 StartY=1.3 StartZ=0 EndX=9.9 EndY=1.3 EndZ=0
    g47: ArcOfCircle CenterX=25.2 CenterY=1.3 CenterZ=0 NormalX=-1e-16 NormalY=0 NormalZ=1 AngleXU=1.5708 Radius=1.5 StartAngle=0 EndAngle=1.5708
    g48: LineSegment StartX=43.8874 StartY=2.8 StartZ=0 EndX=25.2 EndY=2.8 EndZ=0
    g49: Circle CenterX=95.6 CenterY=-57.3 CenterZ=0 NormalX=-1e-16 NormalY=0 NormalZ=1 AngleXU=-1.5708 Radius=1.1
    g50: ArcOfCircle CenterX=60.7 CenterY=-66.9 CenterZ=0 NormalX=-1e-16 NormalY=0 NormalZ=1 AngleXU=-3.14159 Radius=1.5 StartAngle=0 EndAngle=1.5708
    g51: LineSegment StartX=59.2 StartY=-66.1 StartZ=0 EndX=59.2 EndY=-66.9 EndZ=0
    g52: LineSegment StartX=51.15 StartY=-66.1 StartZ=0 EndX=59.2 EndY=-66.1 EndZ=0
    g53: LineSegment StartX=51.15 StartY=-67.6 StartZ=0 EndX=51.15 EndY=-66.1 EndZ=0
    g54: LineSegment StartX=56.7 StartY=-67.6 StartZ=0 EndX=51.15 EndY=-67.6 EndZ=0
    g55: LineSegment StartX=56.7 StartY=-69.9 StartZ=0 EndX=56.7 EndY=-67.6 EndZ=0
    g56: LineSegment StartX=67.1 StartY=-69.9 StartZ=0 EndX=56.7 EndY=-69.9 EndZ=0
    g57: LineSegment StartX=67.1 StartY=-68.4 StartZ=0 EndX=67.1 EndY=-69.9 EndZ=0
    g58: LineSegment StartX=60.7 StartY=-68.4 StartZ=0 EndX=67.1 EndY=-68.4 EndZ=0
    g59: LineSegment StartX=62.7 StartY=-60 StartZ=0 EndX=27.8 EndY=-60 EndZ=0
    g60: LineSegment StartX=62.7 StartY=-57.6 StartZ=0 EndX=62.7 EndY=-60 EndZ=0
    g61: LineSegment StartX=27.8 StartY=-57.6 StartZ=0 EndX=62.7 EndY=-57.6 EndZ=0
    g62: LineSegment StartX=27.8 StartY=-60 StartZ=0 EndX=27.8 EndY=-57.6 EndZ=0
    g63: Circle CenterX=-14 CenterY=-73.8 CenterZ=0 NormalX=-1e-16 NormalY=0 NormalZ=1 AngleXU=-1.5708 Radius=1.1
    g64: LineSegment StartX=-14.8 StartY=-64.1 StartZ=0 EndX=-16.4 EndY=-64.1 EndZ=0
    g65: LineSegment StartX=-14.8 StartY=-54 StartZ=0 EndX=-14.8 EndY=-64.1 EndZ=0
    g66: LineSegment StartX=-16.4 StartY=-54 StartZ=0 EndX=-14.8 EndY=-54 EndZ=0
    g67: LineSegment StartX=-16.4 StartY=-64.1 StartZ=0 EndX=-16.4 EndY=-54 EndZ=0
    g68: LineSegment StartX=52 StartY=-56.2 StartZ=0 EndX=27.8 EndY=-56.2 EndZ=0
    g69: LineSegment StartX=52 StartY=-53.8 StartZ=0 EndX=52 EndY=-56.2 EndZ=0
    g70: LineSegment StartX=27.8 StartY=-53.8 StartZ=0 EndX=52 EndY=-53.8 EndZ=0
    g71: LineSegment StartX=27.8 StartY=-56.2 StartZ=0 EndX=27.8 EndY=-53.8 EndZ=0
    g72: Circle CenterX=95.6 CenterY=-23.3 CenterZ=0 NormalX=-1e-16 NormalY=0 NormalZ=1 AngleXU=-1.5708 Radius=1.1
    g73: Circle CenterX=25.9 CenterY=0.6 CenterZ=0 NormalX=-1e-16 NormalY=0 NormalZ=1 AngleXU=-1.5708 Radius=1.1
  constraints (144):
    c: Coincident(g34,g35)
    c: Coincident(g35,g36)
    c: Coincident(g64,g67)
    c: Coincident(g66,g67)
    c: Coincident(g37,g38)
    c: Coincident(g36,g37)
    c: Coincident(g64,g65)
    c: Coincident(g65,g66)
    c: Coincident(g38,g39)
    c: Coincident(g39,g40)
    c: Coincident(g33,g34)
    c: Coincident(g32,g33)
    c: Coincident(g41,g42)
    c: Coincident(g40,g41)
    c: Coincident(g42,g43)
    c: Coincident(g43,g44)
    c: Coincident(g31,g32)
    c: Coincident(g44,g45)
    c: Coincident(g45,g46)
    c: Coincident(g46,g47)
    c: Coincident(g30,g31)
    c: Coincident(g47,g48)
    c: Coincident(g59,g62)
    c: Coincident(g61,g62)
    c: Coincident(g68,g71)
    c: Coincident(g70,g71)
    c: Coincident(g29,g30)
    c: Coincident(g28,g29)
    c: Coincident(g27,g28)
    c: Coincident(g26,g27)
    c: Coincident(g2,g48)
    c: Coincident(g0,g2)
    c: Coincident(g22,g23)
    c: Coincident(g23,g24)
    c: Coincident(g0,g1)
    c: Coincident(g21,g22)
    c: Coincident(g24,g25)
    c: Coincident(g25,g26)
    c: Coincident(g53,g54)
    c: Coincident(g52,g53)
    c: Coincident(g68,g69)
    c: Coincident(g69,g70)
    c: Coincident(g55,g56)
    c: Coincident(g54,g55)
    c: Coincident(g50,g51)
    c: Coincident(g51,g52)
    c: Coincident(g1,g3)
    c: Coincident(g50,g58)
    c: Coincident(g4,g5)
    c: Coincident(g3,g4)
    c: Coincident(g59,g60)
    c: Coincident(g60,g61)
    c: Coincident(g56,g57)
    c: Coincident(g57,g58)
    c: Coincident(g17,g18)
    c: Coincident(g16,g17)
    c: Coincident(g20,g21)
    c: Coincident(g19,g20)
    c: Coincident(g18,g19)
    c: Coincident(g5,g6)
    c: Coincident(g14,g15)
    c: Coincident(g15,g16)
    c: Coincident(g7,g8)
    c: Coincident(g6,g7)
    c: Coincident(g13,g14)
    c: Coincident(g12,g13)
    c: Coincident(g8,g9)
    c: Coincident(g11,g12)
    c: Coincident(g10,g11)
    c: Coincident(g9,g10)
    c: Block(g0)
    c: Block(g1)
    c: Block(g2)
    c: Block(g3)
    c: Block(g4)
    c: Block(g5)
    c: Block(g6)
    c: Block(g7)
    c: Block(g8)
    c: Block(g9)
    c: Block(g10)
    c: Block(g11)
    c: Block(g12)
    c: Block(g13)
    c: Block(g14)
    c: Block(g15)
    c: Block(g16)
    c: Block(g17)
    c: Block(g18)
    c: Block(g19)
    c: Block(g20)
    c: Block(g21)
    c: Block(g22)
    c: Block(g23)
    c: Block(g24)
    c: Block(g25)
    c: Block(g26)
    c: Block(g27)
    c: Block(g28)
    c: Block(g29)
    c: Block(g30)
    c: Block(g31)
    c: Block(g32)
    c: Block(g33)
    c: Block(g34)
    c: Block(g35)
    c: Block(g36)
    c: Block(g37)
    c: Block(g38)
    c: Block(g39)
    c: Block(g40)
    c: Block(g41)
    c: Block(g42)
    c: Block(g43)
    c: Block(g44)
    c: Block(g45)
    c: Block(g46)
    c: Block(g47)
    c: Block(g48)
    c: Block(g49)
    c: Block(g50)
    c: Block(g51)
    c: Block(g52)
    c: Block(g53)
    c: Block(g54)
    c: Block(g55)
    c: Block(g56)
    c: Block(g57)
    c: Block(g58)
    c: Block(g59)
    c: Block(g60)
    c: Block(g61)
    c: Block(g62)
    c: Block(g63)
    c: Block(g64)
    c: Block(g65)
    c: Block(g66)
    c: Block(g67)
    c: Block(g68)
    c: Block(g69)
    c: Block(g70)
    c: Block(g71)
    c: Block(g72)
    c: Block(g73)
FEATURE [Sketcher::SketchObject] Sketch023
  ArcFitTolerance = 1e-06
  AttachmentOffset = pos=(0,0,-5.1) rot=(0,0,1;0rad)
  AttachmentSupport = -> [XY_Plane004]
  ExternalTypes = [0]
  FullyConstrained = false
  MakeInternals = false
  MapMode = 5
  Placement = pos=(0,0,-5.1) rot=(0,0,1;0rad)
  _ExternalGeoVersion = 0
  sketch-geometry (100):
    g0: ArcOfCircle [constr] CenterX=45.3 CenterY=2.4 CenterZ=0 NormalX=-1e-16 NormalY=0 NormalZ=1 AngleXU=1.5708 Radius=1.5 StartAngle=0 EndAngle=1.22777
    g1: LineSegment [constr] StartX=59.4 StartY=3.9 StartZ=0 EndX=45.3 EndY=3.9 EndZ=0
    g2: LineSegment [constr] StartX=43.8874 StartY=2.9045 StartZ=0 EndX=43.8874 EndY=2.8 EndZ=0
    g3: ArcOfCircle [constr] CenterX=59.4 CenterY=2.4 CenterZ=0 NormalX=-1e-16 NormalY=0 NormalZ=1 AngleXU=3.90995e-07 Radius=1.5 StartAngle=0 EndAngle=1.5708
    g4: LineSegment [constr] StartX=60.9 StartY=-0.4 StartZ=0 EndX=60.9 EndY=2.4 EndZ=0
    g5: LineSegment [constr] StartX=76.4 StartY=-0.4 StartZ=0 EndX=60.9 EndY=-0.4 EndZ=0
    g6: ArcOfCircle [constr] CenterX=76.4 CenterY=-1.9 CenterZ=0 NormalX=-1e-16 NormalY=0 NormalZ=1 AngleXU=3.90995e-07 Radius=1.5 StartAngle=0 EndAngle=1.5708
    g7: LineSegment [constr] StartX=77.9 StartY=-6.3 StartZ=0 EndX=77.9 EndY=-1.9 EndZ=0
    g8: LineSegment [constr] StartX=96.4 StartY=-6.3 StartZ=0 EndX=77.9 EndY=-6.3 EndZ=0
    g9: ArcOfCircle [constr] CenterX=96.4 CenterY=-7.8 CenterZ=0 NormalX=-1e-16 NormalY=0 NormalZ=1 AngleXU=3.90995e-07 Radius=1.5 StartAngle=0 EndAngle=1.5708
    g10: LineSegment [constr] StartX=97.9 StartY=-59.8 StartZ=0 EndX=97.9 EndY=-7.8 EndZ=0
    g11: LineSegment [constr] StartX=97.9 StartY=-72.8 StartZ=0 EndX=97.9 EndY=-59.8 EndZ=0
    g12: ArcOfCircle [constr] CenterX=96.4 CenterY=-72.8 CenterZ=0 NormalX=-1e-16 NormalY=0 NormalZ=1 AngleXU=-1.5708 Radius=1.5 StartAngle=0 EndAngle=1.5708
    g13: LineSegment [constr] StartX=78 StartY=-74.3 StartZ=0 EndX=96.4 EndY=-74.3 EndZ=0
    g14: ArcOfCircle [constr] CenterX=78 CenterY=-72.8 CenterZ=0 NormalX=-1e-16 NormalY=0 NormalZ=1 AngleXU=-3.14159 Radius=1.5 StartAngle=0 EndAngle=1.5708
    g15: LineSegment [constr] StartX=76.5 StartY=-68.4 StartZ=0 EndX=76.5 EndY=-72.8 EndZ=0
    g16: LineSegment [constr] StartX=68.6 StartY=-68.4 StartZ=0 EndX=76.5 EndY=-68.4 EndZ=0
    g17: LineSegment [constr] StartX=43.1 StartY=-66.1 StartZ=0 EndX=49.65 EndY=-66.1 EndZ=0
    g18: LineSegment [constr] StartX=43.1 StartY=-71.2 StartZ=0 EndX=43.1 EndY=-66.1 EndZ=0
    g19: ArcOfCircle [constr] CenterX=41.6 CenterY=-71.2 CenterZ=0 NormalX=-1e-16 NormalY=0 NormalZ=1 AngleXU=-1.5708 Radius=1.5 StartAngle=0 EndAngle=1.5708
    g20: LineSegment [constr] StartX=41.4 StartY=-72.7 StartZ=0 EndX=41.6 EndY=-72.7 EndZ=0
    g21: LineSegment [constr] StartX=24.227 StartY=-72.7043 StartZ=0 EndX=41.4 EndY=-72.7 EndZ=0
    g22: LineSegment [constr] StartX=6.18739 StartY=-75.9853 StartZ=0 EndX=24.227 EndY=-72.7043 EndZ=0
    g23: LineSegment [constr] StartX=-12.4977 StartY=-82.7894 StartZ=0 EndX=6.18739 EndY=-75.9853 EndZ=0
    g24: ArcOfCircle [constr] CenterX=-13.011 CenterY=-81.3799 CenterZ=0 NormalX=-1e-16 NormalY=0 NormalZ=1 AngleXU=-2.78726 Radius=1.5 StartAngle=0 EndAngle=1.56568
    g25: LineSegment [constr] StartX=-22.1 StartY=-61.1344 StartZ=0 EndX=-14.4178 EndY=-81.9004 EndZ=0
    g26: LineSegment [constr] StartX=-22.1 StartY=0 StartZ=0 EndX=-22.1 EndY=-61.1344 EndZ=0
    g27: LineSegment [constr] StartX=9.9 StartY=0 StartZ=0 EndX=5 EndY=0 EndZ=0
    g28: LineSegment [constr] StartX=9.9 StartY=1.3 StartZ=0 EndX=9.9 EndY=0 EndZ=0
    g29: LineSegment [constr] StartX=23.7 StartY=1.3 StartZ=0 EndX=9.9 EndY=1.3 EndZ=0
    g30: ArcOfCircle [constr] CenterX=25.2 CenterY=1.3 CenterZ=0 NormalX=-1e-16 NormalY=0 NormalZ=1 AngleXU=1.5708 Radius=1.5 StartAngle=0 EndAngle=1.5708
    g31: LineSegment [constr] StartX=43.8874 StartY=2.8 StartZ=0 EndX=25.2 EndY=2.8 EndZ=0
    g32: Circle [constr] CenterX=95.6 CenterY=-57.3 CenterZ=0 NormalX=-1e-16 NormalY=0 NormalZ=1 AngleXU=-1.5708 Radius=1.1
    g33: ArcOfCircle [constr] CenterX=60.7 CenterY=-66.9 CenterZ=0 NormalX=-1e-16 NormalY=0 NormalZ=1 AngleXU=-3.14159 Radius=1.5 StartAngle=0 EndAngle=1.5708
    g34: LineSegment [constr] StartX=59.2 StartY=-66.1 StartZ=0 EndX=59.2 EndY=-66.9 EndZ=0
    g35: LineSegment [constr] StartX=51.15 StartY=-66.1 StartZ=0 EndX=59.2 EndY=-66.1 EndZ=0
    g36: LineSegment [constr] StartX=60.7 StartY=-68.4 StartZ=0 EndX=67.1 EndY=-68.4 EndZ=0
    g37: LineSegment [constr] StartX=62.7 StartY=-60 StartZ=0 EndX=27.8 EndY=-60 EndZ=0
    g38: LineSegment [constr] StartX=62.7 StartY=-57.6 StartZ=0 EndX=62.7 EndY=-60 EndZ=0
    g39: LineSegment [constr] StartX=27.8 StartY=-57.6 StartZ=0 EndX=62.7 EndY=-57.6 EndZ=0
    g40: LineSegment [constr] StartX=27.8 StartY=-60 StartZ=0 EndX=27.8 EndY=-57.6 EndZ=0
    g41: Circle [constr] CenterX=-14 CenterY=-73.8 CenterZ=0 NormalX=-1e-16 NormalY=0 NormalZ=1 AngleXU=-1.5708 Radius=1.1
    g42: LineSegment [constr] StartX=-14.8 StartY=-64.1 StartZ=0 EndX=-16.4 EndY=-64.1 EndZ=0
    g43: LineSegment [constr] StartX=-14.8 StartY=-54 StartZ=0 EndX=-14.8 EndY=-64.1 EndZ=0
    g44: LineSegment [constr] StartX=-16.4 StartY=-54 StartZ=0 EndX=-14.8 EndY=-54 EndZ=0
    g45: LineSegment [constr] StartX=-16.4 StartY=-64.1 StartZ=0 EndX=-16.4 EndY=-54 EndZ=0
    g46: LineSegment [constr] StartX=52 StartY=-56.2 StartZ=0 EndX=27.8 EndY=-56.2 EndZ=0
    g47: LineSegment [constr] StartX=52 StartY=-53.8 StartZ=0 EndX=52 EndY=-56.2 EndZ=0
    g48: LineSegment [constr] StartX=27.8 StartY=-53.8 StartZ=0 EndX=52 EndY=-53.8 EndZ=0
    g49: LineSegment [constr] StartX=27.8 StartY=-56.2 StartZ=0 EndX=27.8 EndY=-53.8 EndZ=0
    g50: Circle [constr] CenterX=95.6 CenterY=-23.3 CenterZ=0 NormalX=-1e-16 NormalY=0 NormalZ=1 AngleXU=-1.5708 Radius=1.1
    g51: Circle [constr] CenterX=25.9 CenterY=0.6 CenterZ=0 NormalX=-1e-16 NormalY=0 NormalZ=1 AngleXU=-1.5708 Radius=1.1
    g52: LineSegment [constr] StartX=49.65 StartY=-66.1 StartZ=0 EndX=51.15 EndY=-66.1 EndZ=0
    g53: LineSegment [constr] StartX=67.1 StartY=-68.4 StartZ=0 EndX=68.6 EndY=-68.4 EndZ=0
    g54: LineSegment [constr] StartX=-22.1 StartY=0 StartZ=0 EndX=5 EndY=0 EndZ=0
    g55: LineSegment StartX=-22.1 StartY=0.3 StartZ=0 EndX=5 EndY=0.3 EndZ=0
    g56: LineSegment StartX=9.6 StartY=0.3 StartZ=0 EndX=5 EndY=0.3 EndZ=0
    g57: LineSegment StartX=9.6 StartY=1.3 StartZ=0 EndX=9.6 EndY=0.3 EndZ=0
    g58: ArcOfCircle CenterX=9.9 CenterY=1.3 CenterZ=0 NormalX=0 NormalY=0 NormalZ=1 AngleXU=0 Radius=0.3 StartAngle=1.5708 EndAngle=3.14159
    g59: LineSegment StartX=23.4252 StartY=1.6 StartZ=0 EndX=9.9 EndY=1.6 EndZ=0
    g60: ArcOfCircle CenterX=25.2 CenterY=1.3 CenterZ=0 NormalX=0 NormalY=0 NormalZ=1 AngleXU=1.5708 Radius=1.8 StartAngle=0 EndAngle=1.40335
    g61: LineSegment StartX=43.6417 StartY=3.1 StartZ=0 EndX=25.2 EndY=3.1 EndZ=0
    g62: ArcOfCircle CenterX=45.3 CenterY=2.4 CenterZ=0 NormalX=0 NormalY=0 NormalZ=1 AngleXU=1.5708 Radius=1.8 StartAngle=0 EndAngle=1.17137
    g63: LineSegment StartX=59.4 StartY=4.2 StartZ=0 EndX=45.3 EndY=4.2 EndZ=0
    g64: ArcOfCircle CenterX=59.4 CenterY=2.4 CenterZ=0 NormalX=0 NormalY=0 NormalZ=1 AngleXU=3.90995e-07 Radius=1.8 StartAngle=-1.8e-15 EndAngle=1.5708
    g65: LineSegment StartX=61.2 StartY=-0.1 StartZ=0 EndX=61.2 EndY=2.4 EndZ=0
    g66: LineSegment StartX=76.4 StartY=-0.1 StartZ=0 EndX=61.2 EndY=-0.1 EndZ=0
    g67: ArcOfCircle CenterX=76.4 CenterY=-1.9 CenterZ=0 NormalX=0 NormalY=0 NormalZ=1 AngleXU=3.90995e-07 Radius=1.8 StartAngle=-1.8e-15 EndAngle=1.5708
    g68: LineSegment StartX=78.2 StartY=-6 StartZ=0 EndX=78.2 EndY=-1.9 EndZ=0
    g69: LineSegment StartX=113.4 StartY=-6 StartZ=0 EndX=78.2 EndY=-6 EndZ=0
    g70: ArcOfCircle CenterX=113.4 CenterY=-7.8 CenterZ=0 NormalX=0 NormalY=0 NormalZ=1 AngleXU=3.90995e-07 Radius=1.8 StartAngle=6.28318 EndAngle=7.85398
    g71: LineSegment StartX=115.2 StartY=-59.8 StartZ=0 EndX=115.2 EndY=-7.8 EndZ=0
    g72: LineSegment StartX=115.2 StartY=-72.8 StartZ=0 EndX=115.2 EndY=-59.8 EndZ=0
    g73: ArcOfCircle CenterX=113.4 CenterY=-72.8 CenterZ=0 NormalX=0 NormalY=0 NormalZ=1 AngleXU=-1.5708 Radius=1.8 StartAngle=6.28318 EndAngle=7.85398
    g74: LineSegment StartX=78 StartY=-74.6 StartZ=0 EndX=113.4 EndY=-74.6 EndZ=0
    g75: ArcOfCircle CenterX=78 CenterY=-72.8 CenterZ=0 NormalX=0 NormalY=0 NormalZ=1 AngleXU=-3.14159 Radius=1.8 StartAngle=3.1e-15 EndAngle=1.5708
    g76: LineSegment StartX=76.2 StartY=-68.7 StartZ=0 EndX=76.2 EndY=-72.8 EndZ=0
    g77: LineSegment StartX=68.6 StartY=-68.7 StartZ=0 EndX=76.2 EndY=-68.7 EndZ=0
    g78: LineSegment StartX=67.1 StartY=-68.7 StartZ=0 EndX=68.6 EndY=-68.7 EndZ=0
    g79: LineSegment StartX=60.7 StartY=-68.7 StartZ=0 EndX=67.1 EndY=-68.7 EndZ=0
    g80: ArcOfCircle CenterX=60.7 CenterY=-66.9 CenterZ=0 NormalX=0 NormalY=0 NormalZ=1 AngleXU=-3.14159 Radius=1.8 StartAngle=0 EndAngle=1.5708
    g81: LineSegment StartX=58.9 StartY=-66.4 StartZ=0 EndX=58.9 EndY=-66.9 EndZ=0
    g82: LineSegment StartX=51.15 StartY=-66.4 StartZ=0 EndX=58.9 EndY=-66.4 EndZ=0
    g83: LineSegment StartX=49.65 StartY=-66.4 StartZ=0 EndX=51.15 EndY=-66.4 EndZ=0
    g84: LineSegment StartX=43.4 StartY=-66.4 StartZ=0 EndX=49.65 EndY=-66.4 EndZ=0
    g85: LineSegment StartX=43.4 StartY=-71.2 StartZ=0 EndX=43.4 EndY=-66.4 EndZ=0
    g86: ArcOfCircle CenterX=41.6 CenterY=-71.2 CenterZ=0 NormalX=0 NormalY=0 NormalZ=1 AngleXU=-1.5708 Radius=1.8 StartAngle=0 EndAngle=1.5708
    g87: LineSegment StartX=41.4 StartY=-73 StartZ=0 EndX=41.6 EndY=-73 EndZ=0
    g88: LineSegment StartX=24.2541 StartY=-73.0043 StartZ=0 EndX=41.4 EndY=-73 EndZ=0
    g89: LineSegment StartX=6.26611 StartY=-76.2759 StartZ=0 EndX=24.2541 EndY=-73.0043 EndZ=0
    g90: LineSegment StartX=-12.3951 StartY=-83.0713 StartZ=0 EndX=6.26611 EndY=-76.2759 EndZ=0
    g91: ArcOfCircle CenterX=-13.011 CenterY=-81.3799 CenterZ=0 NormalX=0 NormalY=0 NormalZ=1 AngleXU=-2.78726 Radius=1.8 StartAngle=6.28319 EndAngle=7.84887
    g92: LineSegment StartX=-22.3814 StartY=-61.2385 StartZ=0 EndX=-14.6992 EndY=-82.0044 EndZ=0
    g93: ArcOfCircle CenterX=-22.1 CenterY=-61.1344 CenterZ=0 NormalX=0 NormalY=0 NormalZ=1 AngleXU=1.5708 Radius=0.3 StartAngle=1.5708 EndAngle=1.92513
    g94: LineSegment StartX=-22.4 StartY=0 StartZ=0 EndX=-22.4 EndY=-61.1344 EndZ=0
    g95: ArcOfCircle CenterX=-22.1 CenterY=0 CenterZ=0 NormalX=0 NormalY=0 NormalZ=1 AngleXU=0 Radius=0.3 StartAngle=1.5708 EndAngle=3.14159
    g96: LineSegment [constr] StartX=113.4 StartY=-7.8 StartZ=0 EndX=113.4 EndY=-6 EndZ=0
    g97: LineSegment [constr] StartX=113.4 StartY=-7.8 StartZ=0 EndX=115.2 EndY=-7.8 EndZ=0
    g98: LineSegment [constr] StartX=113.4 StartY=-72.8 StartZ=0 EndX=113.4 EndY=-74.6 EndZ=0
    g99: LineSegment [constr] StartX=113.4 StartY=-72.8 StartZ=0 EndX=115.2 EndY=-72.8 EndZ=0
  constraints (168):
    c: Coincident(g25,g26)
    c: Coincident(g42,g45)
    c: Coincident(g44,g45)
    c: Coincident(g42,g43)
    c: Coincident(g43,g44)
    c: Coincident(g24,g25)
    c: Coincident(g23,g24)
    c: Coincident(g22,g23)
    c: Coincident(g27,g28)
    c: Coincident(g28,g29)
    c: Coincident(g29,g30)
    c: Coincident(g21,g22)
    c: Coincident(g30,g31)
    c: Coincident(g37,g40)
    c: Coincident(g39,g40)
    c: Coincident(g46,g49)
    c: Coincident(g48,g49)
    c: Coincident(g20,g21)
    c: Coincident(g19,g20)
    c: Coincident(g18,g19)
    c: Coincident(g17,g18)
    c: Coincident(g2,g31)
    c: Coincident(g0,g2)
    c: Coincident(g0,g1)
    c: Coincident(g46,g47)
    c: Coincident(g47,g48)
    c: Coincident(g33,g34)
    c: Coincident(g34,g35)
    c: Coincident(g1,g3)
    c: Coincident(g33,g36)
    c: Coincident(g4,g5)
    c: Coincident(g3,g4)
    c: Coincident(g37,g38)
    c: Coincident(g38,g39)
    c: Coincident(g5,g6)
    c: Coincident(g14,g15)
    c: Coincident(g15,g16)
    c: Coincident(g7,g8)
    c: Coincident(g6,g7)
    c: Coincident(g13,g14)
    c: Coincident(g12,g13)
    c: Coincident(g8,g9)
    c: Coincident(g11,g12)
    c: Coincident(g10,g11)
    c: Coincident(g9,g10)
    c: Block(g0)
    c: Block(g1)
    c: Block(g2)
    c: Block(g3)
    c: Block(g4)
    c: Block(g5)
    c: Block(g6)
    c: Block(g7)
    c: Block(g8)
    c: Block(g9)
    c: Block(g10)
    c: Block(g11)
    c: Block(g12)
    c: Block(g13)
    c: Block(g14)
    c: Block(g15)
    c: Block(g16)
    c: Block(g17)
    c: Block(g18)
    c: Block(g19)
    c: Block(g20)
    c: Block(g21)
    c: Block(g22)
    c: Block(g23)
    c: Block(g24)
    c: Block(g25)
    c: Block(g26)
    c: Block(g27)
    c: Block(g28)
    c: Block(g29)
    c: Block(g30)
    c: Block(g31)
    c: Block(g32)
    c: Block(g33)
    c: Block(g34)
    c: Block(g35)
    c: Block(g36)
    c: Block(g37)
    c: Block(g38)
    c: Block(g39)
    c: Block(g40)
    c: Block(g41)
    c: Block(g42)
    c: Block(g43)
    c: Block(g44)
    c: Block(g45)
    c: Block(g46)
    c: Block(g47)
    c: Block(g48)
    c: Block(g49)
    c: Block(g50)
    c: Block(g51)
    c: Coincident(g52,g17)
    c: Coincident(g52,g35)
    c: Horizontal(g52)
    c: Coincident(g53,g36)
    c: Coincident(g53,g16)
    c: Horizontal(g53)
    c: Coincident(g54,g26)
    c: Coincident(g54,g27)
    c: Horizontal(g54)
    c: Coincident(g55,g56)
    c: Tangent(g55,g95) = 1.5708
    c: Coincident(g56,g57)
    c: Tangent(g57,g58) = -1.5708
    c: Tangent(g58,g59) = -1.5708
    c: Coincident(g59,g60)
    c: Coincident(g61,g62)
    c: Coincident(g62,g63)
    c: Coincident(g65,g66)
    c: Coincident(g68,g69)
    c: Coincident(g71,g72)
    c: Coincident(g76,g77)
    c: Coincident(g77,g78)
    c: Coincident(g78,g79)
    c: Coincident(g81,g82)
    c: Coincident(g82,g83)
    c: Coincident(g83,g84)
    c: Coincident(g84,g85)
    c: Coincident(g87,g88)
    c: Coincident(g88,g89)
    c: Coincident(g89,g90)
    c: Tangent(g92,g93) = -1.5708
    c: Tangent(g93,g94) = -1.5708
    c: Tangent(g94,g95) = -1.5708
    c: Coincident(g91,g92)
    c: Coincident(g90,g91)
    c: Coincident(g60,g61)
    c: Coincident(g86,g87)
    c: Coincident(g85,g86)
    c: Coincident(g80,g81)
    c: Coincident(g63,g64)
    c: Coincident(g79,g80)
    c: Coincident(g64,g65)
    c: Coincident(g66,g67)
    c: Coincident(g74,g75)
    c: Coincident(g67,g68)
    c: Coincident(g73,g74)
    c: Coincident(g69,g70)
    c: Coincident(g72,g73)
    c: Coincident(g70,g71)
    c: Block(g68)
    c: Block(g75)
    c: Block(g76)
    c: Radius(g73) = 1.8
    c: Radius(g70) = 1.8
    c: Horizontal(g69)
    c: Horizontal(g74)
    c: Vertical(g72)
    c: Vertical(g71)
    c: DistanceX(g-1,g72) = 115.2
    c: Coincident(g96,g70)
    c: Coincident(g96,g69)
    c: Vertical(g96)
    c: Coincident(g97,g70)
    c: Coincident(g97,g70)
    c: Horizontal(g97)
    c: Coincident(g98,g73)
    c: Coincident(g98,g73)
    c: Vertical(g98)
    c: Coincident(g99,g73)
    c: Coincident(g99,g72)
    c: Horizontal(g99)
FEATURE [PartDesign::Pocket] Pocket008
  BaseFeature = -> Pad010
  Direction = (0,0,-1)
  Length = 10
  Length2 = 5
  Profile = -> Sketch023
  ReferenceAxis = -> Sketch023 [N_Axis]
  Refine = true
  Reversed = true
  SideType = 0
  Suppressed = false
  Type = 0
  Type2 = 0
FEATURE [Sketcher::SketchObject] Sketch024
  ArcFitTolerance = 1e-06
  AttachmentOffset = pos=(0,0,-5.1) rot=(0,0,1;0rad)
  AttachmentSupport = -> [XY_Plane004]
  ExternalTypes = [0]
  FullyConstrained = false
  MakeInternals = false
  MapMode = 5
  Placement = pos=(0,0,-5.1) rot=(0,0,1;0rad)
  _ExternalGeoVersion = 0
  sketch-geometry (4):
    g0: LineSegment StartX=9.9 StartY=0 StartZ=0 EndX=9.9 EndY=7.12941 EndZ=0
    g1: LineSegment StartX=9.9 StartY=7.12941 StartZ=0 EndX=2.38364 EndY=7.12941 EndZ=0
    g2: LineSegment StartX=2.38364 StartY=7.12941 StartZ=0 EndX=2.38364 EndY=0 EndZ=0
    g3: LineSegment StartX=2.38364 StartY=0 StartZ=0 EndX=9.9 EndY=0 EndZ=0
  constraints (10):
    c: Coincident(g0,g1)
    c: Coincident(g1,g2)
    c: Coincident(g2,g3)
    c: Coincident(g3,g0)
    c: Vertical(g0)
    c: Vertical(g2)
    c: Horizontal(g1)
    c: Horizontal(g3)
    c: DistanceX(g-1,g0) = 9.9
    c: PointOnObject(g2,g-1)
FEATURE [PartDesign::Pocket] Pocket009
  BaseFeature = -> Pocket008
  Direction = (0,0,-1)
  Length = 10
  Length2 = 10
  Profile = -> Sketch024
  ReferenceAxis = -> Sketch024 [N_Axis]
  Refine = true
  SideType = 1
  Suppressed = false
  Type = 0
  Type2 = 0
FEATURE [Sketcher::SketchObject] Sketch025
  ArcFitTolerance = 1e-06
  AttachmentSupport = -> [XY_Plane004]
  ExternalTypes = [0]
  FullyConstrained = false
  MakeInternals = false
  MapMode = 5
  _ExternalGeoVersion = 0
  sketch-geometry (79):
    g0: ArcOfCircle [constr] CenterX=45.3 CenterY=2.4 CenterZ=0 NormalX=-1e-16 NormalY=0 NormalZ=1 AngleXU=1.5708 Radius=1.5 StartAngle=0 EndAngle=1.22777
    g1: LineSegment [constr] StartX=59.4 StartY=3.9 StartZ=0 EndX=45.3 EndY=3.9 EndZ=0
    g2: LineSegment [constr] StartX=43.8874 StartY=2.9045 StartZ=0 EndX=43.8874 EndY=2.8 EndZ=0
    g3: ArcOfCircle [constr] CenterX=59.4 CenterY=2.4 CenterZ=0 NormalX=-1e-16 NormalY=0 NormalZ=1 AngleXU=3.90995e-07 Radius=1.5 StartAngle=0 EndAngle=1.5708
    g4: LineSegment [constr] StartX=60.9 StartY=-0.4 StartZ=0 EndX=60.9 EndY=2.4 EndZ=0
    g5: LineSegment [constr] StartX=76.4 StartY=-0.4 StartZ=0 EndX=60.9 EndY=-0.4 EndZ=0
    g6: ArcOfCircle [constr] CenterX=76.4 CenterY=-1.9 CenterZ=0 NormalX=-1e-16 NormalY=0 NormalZ=1 AngleXU=3.90995e-07 Radius=1.5 StartAngle=0 EndAngle=1.5708
    g7: LineSegment [constr] StartX=77.9 StartY=-6.3 StartZ=0 EndX=77.9 EndY=-1.9 EndZ=0
    g8: LineSegment [constr] StartX=96.4 StartY=-6.3 StartZ=0 EndX=77.9 EndY=-6.3 EndZ=0
    g9: ArcOfCircle [constr] CenterX=96.4 CenterY=-7.8 CenterZ=0 NormalX=-1e-16 NormalY=0 NormalZ=1 AngleXU=3.90995e-07 Radius=1.5 StartAngle=0 EndAngle=1.5708
    g10: LineSegment [constr] StartX=97.9 StartY=-59.8 StartZ=0 EndX=97.9 EndY=-7.8 EndZ=0
    g11: LineSegment [constr] StartX=97.9 StartY=-72.8 StartZ=0 EndX=97.9 EndY=-59.8 EndZ=0
    g12: ArcOfCircle [constr] CenterX=96.4 CenterY=-72.8 CenterZ=0 NormalX=-1e-16 NormalY=0 NormalZ=1 AngleXU=-1.5708 Radius=1.5 StartAngle=0 EndAngle=1.5708
    g13: LineSegment [constr] StartX=78 StartY=-74.3 StartZ=0 EndX=96.4 EndY=-74.3 EndZ=0
    g14: ArcOfCircle [constr] CenterX=78 CenterY=-72.8 CenterZ=0 NormalX=-1e-16 NormalY=0 NormalZ=1 AngleXU=-3.14159 Radius=1.5 StartAngle=0 EndAngle=1.5708
    g15: LineSegment [constr] StartX=76.5 StartY=-68.4 StartZ=0 EndX=76.5 EndY=-72.8 EndZ=0
    g16: LineSegment [constr] StartX=68.6 StartY=-68.4 StartZ=0 EndX=76.5 EndY=-68.4 EndZ=0
    g17: LineSegment [constr] StartX=68.6 StartY=-69.9 StartZ=0 EndX=68.6 EndY=-68.4 EndZ=0
    g18: LineSegment [constr] StartX=75 StartY=-69.9 StartZ=0 EndX=68.6 EndY=-69.9 EndZ=0
    g19: LineSegment [constr] StartX=75 StartY=-72.8 StartZ=0 EndX=75 EndY=-69.9 EndZ=0
    g20: ArcOfCircle [constr] CenterX=73.5 CenterY=-72.8 CenterZ=0 NormalX=-1e-16 NormalY=0 NormalZ=1 AngleXU=-1.5708 Radius=1.5 StartAngle=0 EndAngle=1.5708
    g21: LineSegment [constr] StartX=46.1 StartY=-74.3 StartZ=0 EndX=73.5 EndY=-74.3 EndZ=0
    g22: ArcOfCircle [constr] CenterX=46.1 CenterY=-72.8 CenterZ=0 NormalX=-1e-16 NormalY=0 NormalZ=1 AngleXU=-3.14159 Radius=1.5 StartAngle=0 EndAngle=1.5708
    g23: LineSegment [constr] StartX=44.6 StartY=-67.6 StartZ=0 EndX=44.6 EndY=-72.8 EndZ=0
    g24: LineSegment [constr] StartX=49.65 StartY=-67.6 StartZ=0 EndX=44.6 EndY=-67.6 EndZ=0
    g25: LineSegment [constr] StartX=49.65 StartY=-66.1 StartZ=0 EndX=49.65 EndY=-67.6 EndZ=0
    g26: LineSegment [constr] StartX=43.1 StartY=-66.1 StartZ=0 EndX=49.65 EndY=-66.1 EndZ=0
    g27: LineSegment [constr] StartX=43.1 StartY=-71.2 StartZ=0 EndX=43.1 EndY=-66.1 EndZ=0
    g28: ArcOfCircle [constr] CenterX=41.6 CenterY=-71.2 CenterZ=0 NormalX=-1e-16 NormalY=0 NormalZ=1 AngleXU=-1.5708 Radius=1.5 StartAngle=0 EndAngle=1.5708
    g29: LineSegment [constr] StartX=41.4 StartY=-72.7 StartZ=0 EndX=41.6 EndY=-72.7 EndZ=0
    g30: LineSegment [constr] StartX=24.227 StartY=-72.7043 StartZ=0 EndX=41.4 EndY=-72.7 EndZ=0
    g31: LineSegment [constr] StartX=6.18739 StartY=-75.9853 StartZ=0 EndX=24.227 EndY=-72.7043 EndZ=0
    g32: LineSegment [constr] StartX=-12.4977 StartY=-82.7894 StartZ=0 EndX=6.18739 EndY=-75.9853 EndZ=0
    g33: ArcOfCircle [constr] CenterX=-13.011 CenterY=-81.3799 CenterZ=0 NormalX=-1e-16 NormalY=0 NormalZ=1 AngleXU=-2.78726 Radius=1.5 StartAngle=0 EndAngle=1.56568
    g34: LineSegment [constr] StartX=-22.1 StartY=-61.1344 StartZ=0 EndX=-14.4178 EndY=-81.9004 EndZ=0
    g35: LineSegment [constr] StartX=-22.1 StartY=0 StartZ=0 EndX=-22.1 EndY=-61.1344 EndZ=0
    g36: LineSegment [constr] StartX=-16.4 StartY=0 StartZ=0 EndX=-22.1 EndY=0 EndZ=0
    g37: LineSegment [constr] StartX=-16.4 StartY=-10.5 StartZ=0 EndX=-16.4 EndY=0 EndZ=0
    g38: LineSegment [constr] StartX=-14.8 StartY=-10.5 StartZ=0 EndX=-16.4 EndY=-10.5 EndZ=0
    g39: LineSegment [constr] StartX=-14.8 StartY=0 StartZ=0 EndX=-14.8 EndY=-10.5 EndZ=0
    g40: LineSegment [constr] StartX=-5 StartY=0 StartZ=0 EndX=-14.8 EndY=0 EndZ=0
    g41: LineSegment [constr] StartX=-5 StartY=-4 StartZ=0 EndX=-5 EndY=0 EndZ=0
    g42: LineSegment [constr] StartX=5 StartY=-4 StartZ=0 EndX=-5 EndY=-4 EndZ=0
    g43: LineSegment [constr] StartX=5 StartY=0 StartZ=0 EndX=5 EndY=-4 EndZ=0
    g44: LineSegment [constr] StartX=9.9 StartY=0 StartZ=0 EndX=5 EndY=0 EndZ=0
    g45: LineSegment [constr] StartX=9.9 StartY=1.3 StartZ=0 EndX=9.9 EndY=0 EndZ=0
    g46: LineSegment [constr] StartX=23.7 StartY=1.3 StartZ=0 EndX=9.9 EndY=1.3 EndZ=0
    g47: ArcOfCircle [constr] CenterX=25.2 CenterY=1.3 CenterZ=0 NormalX=-1e-16 NormalY=0 NormalZ=1 AngleXU=1.5708 Radius=1.5 StartAngle=0 EndAngle=1.5708
    g48: LineSegment [constr] StartX=43.8874 StartY=2.8 StartZ=0 EndX=25.2 EndY=2.8 EndZ=0
    g49: Circle [constr] CenterX=112.6 CenterY=-57.3 CenterZ=0 NormalX=-1e-16 NormalY=0 NormalZ=1 AngleXU=-1.5708 Radius=1.1
    g50: ArcOfCircle [constr] CenterX=60.7 CenterY=-66.9 CenterZ=0 NormalX=-1e-16 NormalY=0 NormalZ=1 AngleXU=-3.14159 Radius=1.5 StartAngle=0 EndAngle=1.5708
    g51: LineSegment [constr] StartX=59.2 StartY=-66.1 StartZ=0 EndX=59.2 EndY=-66.9 EndZ=0
    g52: LineSegment [constr] StartX=51.15 StartY=-66.1 StartZ=0 EndX=59.2 EndY=-66.1 EndZ=0
    g53: LineSegment [constr] StartX=51.15 StartY=-67.6 StartZ=0 EndX=51.15 EndY=-66.1 EndZ=0
    g54: LineSegment [constr] StartX=56.7 StartY=-67.6 StartZ=0 EndX=51.15 EndY=-67.6 EndZ=0
    g55: LineSegment [constr] StartX=56.7 StartY=-69.9 StartZ=0 EndX=56.7 EndY=-67.6 EndZ=0
    g56: LineSegment [constr] StartX=67.1 StartY=-69.9 StartZ=0 EndX=56.7 EndY=-69.9 EndZ=0
    g57: LineSegment [constr] StartX=67.1 StartY=-68.4 StartZ=0 EndX=67.1 EndY=-69.9 EndZ=0
    g58: LineSegment [constr] StartX=60.7 StartY=-68.4 StartZ=0 EndX=67.1 EndY=-68.4 EndZ=0
    g59: LineSegment [constr] StartX=62.7 StartY=-60 StartZ=0 EndX=27.8 EndY=-60 EndZ=0
    g60: LineSegment [constr] StartX=62.7 StartY=-57.6 StartZ=0 EndX=62.7 EndY=-60 EndZ=0
    g61: LineSegment [constr] StartX=27.8 StartY=-57.6 StartZ=0 EndX=62.7 EndY=-57.6 EndZ=0
    g62: LineSegment [constr] StartX=27.8 StartY=-60 StartZ=0 EndX=27.8 EndY=-57.6 EndZ=0
    g63: Circle [constr] CenterX=-14 CenterY=-73.8 CenterZ=0 NormalX=-1e-16 NormalY=0 NormalZ=1 AngleXU=-1.5708 Radius=1.1
    g64: LineSegment [constr] StartX=-14.8 StartY=-64.1 StartZ=0 EndX=-16.4 EndY=-64.1 EndZ=0
    g65: LineSegment [constr] StartX=-14.8 StartY=-54 StartZ=0 EndX=-14.8 EndY=-64.1 EndZ=0
    g66: LineSegment [constr] StartX=-16.4 StartY=-54 StartZ=0 EndX=-14.8 EndY=-54 EndZ=0
    g67: LineSegment [constr] StartX=-16.4 StartY=-64.1 StartZ=0 EndX=-16.4 EndY=-54 EndZ=0
    g68: LineSegment [constr] StartX=52 StartY=-56.2 StartZ=0 EndX=27.8 EndY=-56.2 EndZ=0
    g69: LineSegment [constr] StartX=52 StartY=-53.8 StartZ=0 EndX=52 EndY=-56.2 EndZ=0
    g70: LineSegment [constr] StartX=27.8 StartY=-53.8 StartZ=0 EndX=52 EndY=-53.8 EndZ=0
    g71: LineSegment [constr] StartX=27.8 StartY=-56.2 StartZ=0 EndX=27.8 EndY=-53.8 EndZ=0
    g72: Circle [constr] CenterX=112.6 CenterY=-23.3 CenterZ=0 NormalX=-1e-16 NormalY=0 NormalZ=1 AngleXU=-1.5708 Radius=1.1
    g73: Circle [constr] CenterX=25.9 CenterY=0.6 CenterZ=0 NormalX=-1e-16 NormalY=0 NormalZ=1 AngleXU=-1.5708 Radius=1.1
    g74: Circle CenterX=25.9 CenterY=0.6 CenterZ=0 NormalX=0 NormalY=0 NormalZ=1 AngleXU=0 Radius=1.2
    g75: Circle CenterX=25.9 CenterY=0.6 CenterZ=0 NormalX=0 NormalY=0 NormalZ=1 AngleXU=0 Radius=1.2
    g76: Circle CenterX=112.6 CenterY=-23.3 CenterZ=0 NormalX=0 NormalY=0 NormalZ=1 AngleXU=0 Radius=1.1
    g77: Circle CenterX=112.6 CenterY=-57.3 CenterZ=0 NormalX=0 NormalY=0 NormalZ=1 AngleXU=0 Radius=1.1
    g78: Circle CenterX=-14 CenterY=-73.8 CenterZ=0 NormalX=0 NormalY=0 NormalZ=1 AngleXU=0 Radius=1.2
  constraints (157):
    c: Coincident(g34,g35)
    c: Coincident(g35,g36)
    c: Coincident(g64,g67)
    c: Coincident(g66,g67)
    c: Coincident(g37,g38)
    c: Coincident(g36,g37)
    c: Coincident(g64,g65)
    c: Coincident(g65,g66)
    c: Coincident(g38,g39)
    c: Coincident(g39,g40)
    c: Coincident(g33,g34)
    c: Coincident(g32,g33)
    c: Coincident(g41,g42)
    c: Coincident(g40,g41)
    c: Coincident(g42,g43)
    c: Coincident(g43,g44)
    c: Coincident(g31,g32)
    c: Coincident(g44,g45)
    c: Coincident(g45,g46)
    c: Coincident(g46,g47)
    c: Coincident(g30,g31)
    c: Coincident(g47,g48)
    c: Coincident(g59,g62)
    c: Coincident(g61,g62)
    c: Coincident(g68,g71)
    c: Coincident(g70,g71)
    c: Coincident(g29,g30)
    c: Coincident(g28,g29)
    c: Coincident(g27,g28)
    c: Coincident(g26,g27)
    c: Coincident(g2,g48)
    c: Coincident(g0,g2)
    c: Coincident(g22,g23)
    c: Coincident(g23,g24)
    c: Coincident(g0,g1)
    c: Coincident(g21,g22)
    c: Coincident(g24,g25)
    c: Coincident(g25,g26)
    c: Coincident(g53,g54)
    c: Coincident(g52,g53)
    c: Coincident(g68,g69)
    c: Coincident(g69,g70)
    c: Coincident(g55,g56)
    c: Coincident(g54,g55)
    c: Coincident(g50,g51)
    c: Coincident(g51,g52)
    c: Coincident(g1,g3)
    c: Coincident(g50,g58)
    c: Coincident(g4,g5)
    c: Coincident(g3,g4)
    c: Coincident(g59,g60)
    c: Coincident(g60,g61)
    c: Coincident(g56,g57)
    c: Coincident(g57,g58)
    c: Coincident(g17,g18)
    c: Coincident(g16,g17)
    c: Coincident(g20,g21)
    c: Coincident(g19,g20)
    c: Coincident(g18,g19)
    c: Coincident(g5,g6)
    c: Coincident(g14,g15)
    c: Coincident(g15,g16)
    c: Coincident(g7,g8)
    c: Coincident(g6,g7)
    c: Coincident(g13,g14)
    c: Coincident(g12,g13)
    c: Coincident(g8,g9)
    c: Coincident(g11,g12)
    c: Coincident(g10,g11)
    c: Coincident(g9,g10)
    c: Block(g0)
    c: Block(g1)
    c: Block(g2)
    c: Block(g3)
    c: Block(g4)
    c: Block(g5)
    c: Block(g6)
    c: Block(g7)
    c: Block(g8)
    c: Block(g9)
    c: Block(g10)
    c: Block(g11)
    c: Block(g12)
    c: Block(g13)
    c: Block(g14)
    c: Block(g15)
    c: Block(g16)
    c: Block(g17)
    c: Block(g18)
    c: Block(g19)
    c: Block(g20)
    c: Block(g21)
    c: Block(g22)
    c: Block(g23)
    c: Block(g24)
    c: Block(g25)
    c: Block(g26)
    c: Block(g27)
    c: Block(g28)
    c: Block(g29)
    c: Block(g30)
    c: Block(g31)
    c: Block(g32)
    c: Block(g33)
    c: Block(g34)
    c: Block(g35)
    c: Block(g36)
    c: Block(g37)
    c: Block(g38)
    c: Block(g39)
    c: Block(g40)
    c: Block(g41)
    c: Block(g42)
    c: Block(g43)
    c: Block(g44)
    c: Block(g45)
    c: Block(g46)
    c: Block(g47)
    c: Block(g48)
    c: Block(g50)
    c: Block(g51)
    c: Block(g52)
    c: Block(g53)
    c: Block(g54)
    c: Block(g55)
    c: Block(g56)
    c: Block(g57)
    c: Block(g58)
    c: Block(g59)
    c: Block(g60)
    c: Block(g61)
    c: Block(g62)
    c: Block(g63)
    c: Block(g64)
    c: Block(g65)
    c: Block(g66)
    c: Block(g67)
    c: Block(g68)
    c: Block(g69)
    c: Block(g70)
    c: Block(g71)
    c: Block(g73)
    c: Diameter(g75) = 2.4
    c: Coincident(g75,g74)
    c: Equal(g75,g74)
    c: Coincident(g76,g72)
    c: Equal(g76,g72)
    c: Coincident(g77,g49)
    c: Equal(g77,g49)
    c: Diameter(g78) = 2.4
    c: Coincident(g78,g63)
    c: Diameter(g76) = 2.2
    c: Diameter(g77) = 2.2
    c: DistanceX(g-1,g72) = 112.6
    c: DistanceY(g72,g-1) = 23.3
    c: DistanceY(g49,g-1) = 57.3
    c: DistanceX(g-1,g49) = 112.6
FEATURE [PartDesign::Pocket] Pocket010
  BaseFeature = -> Pocket009
  Direction = (0,0,-1)
  Length = 20
  Length2 = 5
  Profile = -> Sketch025
  ReferenceAxis = -> Sketch025 [N_Axis]
  Refine = true
  SideType = 0
  Suppressed = false
  Type = 0
  Type2 = 0
FEATURE [PartDesign::Fillet] Fillet
  Base = -> Pocket010 [Edge100,Edge95,Edge85]
  BaseFeature = -> Pocket010
  Radius = 1
  Refine = true
  SupportTransform = false
  Suppressed = false
  UseAllEdges = false
FEATURE [PartDesign::Fillet] Fillet002
  Base = -> Fillet [Edge157,Edge179,Edge180,Edge175,Edge165,Edge168,Edge164,Edge57]
  BaseFeature = -> Fillet
  Radius = 0.499
  Refine = true
  SupportTransform = false
  Suppressed = false
  UseAllEdges = false
FEATURE [Sketcher::SketchObject] Sketch027
  ArcFitTolerance = 1e-06
  AttachmentOffset = pos=(0,0,-5.9) rot=(0,0,1;0rad)
  AttachmentSupport = -> [XY_Plane004]
  ExternalTypes = [0]
  FullyConstrained = false
  MakeInternals = false
  MapMode = 5
  Placement = pos=(0,0,-5.9) rot=(0,0,1;0rad)
  _ExternalGeoVersion = 0
  expr: Constraints[142] = Sketch025.Constraints[142]
  expr: Constraints[149] = Sketch025.Constraints[149]
  sketch-geometry (83):
    g0: ArcOfCircle [constr] CenterX=45.3 CenterY=2.4 CenterZ=0 NormalX=-1e-16 NormalY=0 NormalZ=1 AngleXU=1.5708 Radius=1.5 StartAngle=0 EndAngle=1.22777
    g1: LineSegment [constr] StartX=59.4 StartY=3.9 StartZ=0 EndX=45.3 EndY=3.9 EndZ=0
    g2: LineSegment [constr] StartX=43.8874 StartY=2.9045 StartZ=0 EndX=43.8874 EndY=2.8 EndZ=0
    g3: ArcOfCircle [constr] CenterX=59.4 CenterY=2.4 CenterZ=0 NormalX=-1e-16 NormalY=0 NormalZ=1 AngleXU=3.90995e-07 Radius=1.5 StartAngle=0 EndAngle=1.5708
    g4: LineSegment [constr] StartX=60.9 StartY=-0.4 StartZ=0 EndX=60.9 EndY=2.4 EndZ=0
    g5: LineSegment [constr] StartX=76.4 StartY=-0.4 StartZ=0 EndX=60.9 EndY=-0.4 EndZ=0
    g6: ArcOfCircle [constr] CenterX=76.4 CenterY=-1.9 CenterZ=0 NormalX=-1e-16 NormalY=0 NormalZ=1 AngleXU=3.90995e-07 Radius=1.5 StartAngle=0 EndAngle=1.5708
    g7: LineSegment [constr] StartX=77.9 StartY=-6.3 StartZ=0 EndX=77.9 EndY=-1.9 EndZ=0
    g8: LineSegment [constr] StartX=96.4 StartY=-6.3 StartZ=0 EndX=77.9 EndY=-6.3 EndZ=0
    g9: ArcOfCircle [constr] CenterX=96.4 CenterY=-7.8 CenterZ=0 NormalX=-1e-16 NormalY=0 NormalZ=1 AngleXU=3.90995e-07 Radius=1.5 StartAngle=0 EndAngle=1.5708
    g10: LineSegment [constr] StartX=97.9 StartY=-59.8 StartZ=0 EndX=97.9 EndY=-7.8 EndZ=0
    g11: LineSegment [constr] StartX=97.9 StartY=-72.8 StartZ=0 EndX=97.9 EndY=-59.8 EndZ=0
    g12: ArcOfCircle [constr] CenterX=96.4 CenterY=-72.8 CenterZ=0 NormalX=-1e-16 NormalY=0 NormalZ=1 AngleXU=-1.5708 Radius=1.5 StartAngle=0 EndAngle=1.5708
    g13: LineSegment [constr] StartX=78 StartY=-74.3 StartZ=0 EndX=96.4 EndY=-74.3 EndZ=0
    g14: ArcOfCircle [constr] CenterX=78 CenterY=-72.8 CenterZ=0 NormalX=-1e-16 NormalY=0 NormalZ=1 AngleXU=-3.14159 Radius=1.5 StartAngle=0 EndAngle=1.5708
    g15: LineSegment [constr] StartX=76.5 StartY=-68.4 StartZ=0 EndX=76.5 EndY=-72.8 EndZ=0
    g16: LineSegment [constr] StartX=68.6 StartY=-68.4 StartZ=0 EndX=76.5 EndY=-68.4 EndZ=0
    g17: LineSegment [constr] StartX=68.6 StartY=-69.9 StartZ=0 EndX=68.6 EndY=-68.4 EndZ=0
    g18: LineSegment [constr] StartX=75 StartY=-69.9 StartZ=0 EndX=68.6 EndY=-69.9 EndZ=0
    g19: LineSegment [constr] StartX=75 StartY=-72.8 StartZ=0 EndX=75 EndY=-69.9 EndZ=0
    g20: ArcOfCircle [constr] CenterX=73.5 CenterY=-72.8 CenterZ=0 NormalX=-1e-16 NormalY=0 NormalZ=1 AngleXU=-1.5708 Radius=1.5 StartAngle=0 EndAngle=1.5708
    g21: LineSegment [constr] StartX=46.1 StartY=-74.3 StartZ=0 EndX=73.5 EndY=-74.3 EndZ=0
    g22: ArcOfCircle [constr] CenterX=46.1 CenterY=-72.8 CenterZ=0 NormalX=-1e-16 NormalY=0 NormalZ=1 AngleXU=-3.14159 Radius=1.5 StartAngle=0 EndAngle=1.5708
    g23: LineSegment [constr] StartX=44.6 StartY=-67.6 StartZ=0 EndX=44.6 EndY=-72.8 EndZ=0
    g24: LineSegment [constr] StartX=49.65 StartY=-67.6 StartZ=0 EndX=44.6 EndY=-67.6 EndZ=0
    g25: LineSegment [constr] StartX=49.65 StartY=-66.1 StartZ=0 EndX=49.65 EndY=-67.6 EndZ=0
    g26: LineSegment [constr] StartX=43.1 StartY=-66.1 StartZ=0 EndX=49.65 EndY=-66.1 EndZ=0
    g27: LineSegment [constr] StartX=43.1 StartY=-71.2 StartZ=0 EndX=43.1 EndY=-66.1 EndZ=0
    g28: ArcOfCircle [constr] CenterX=41.6 CenterY=-71.2 CenterZ=0 NormalX=-1e-16 NormalY=0 NormalZ=1 AngleXU=-1.5708 Radius=1.5 StartAngle=0 EndAngle=1.5708
    g29: LineSegment [constr] StartX=41.4 StartY=-72.7 StartZ=0 EndX=41.6 EndY=-72.7 EndZ=0
    g30: LineSegment [constr] StartX=24.227 StartY=-72.7043 StartZ=0 EndX=41.4 EndY=-72.7 EndZ=0
    g31: LineSegment [constr] StartX=6.18739 StartY=-75.9853 StartZ=0 EndX=24.227 EndY=-72.7043 EndZ=0
    g32: LineSegment [constr] StartX=-12.4977 StartY=-82.7894 StartZ=0 EndX=6.18739 EndY=-75.9853 EndZ=0
    g33: ArcOfCircle [constr] CenterX=-13.011 CenterY=-81.3799 CenterZ=0 NormalX=-1e-16 NormalY=0 NormalZ=1 AngleXU=-2.78726 Radius=1.5 StartAngle=0 EndAngle=1.56568
    g34: LineSegment [constr] StartX=-22.1 StartY=-61.1344 StartZ=0 EndX=-14.4178 EndY=-81.9004 EndZ=0
    g35: LineSegment [constr] StartX=-22.1 StartY=0 StartZ=0 EndX=-22.1 EndY=-61.1344 EndZ=0
    g36: LineSegment [constr] StartX=-16.4 StartY=0 StartZ=0 EndX=-22.1 EndY=0 EndZ=0
    g37: LineSegment [constr] StartX=-16.4 StartY=-10.5 StartZ=0 EndX=-16.4 EndY=0 EndZ=0
    g38: LineSegment [constr] StartX=-14.8 StartY=-10.5 StartZ=0 EndX=-16.4 EndY=-10.5 EndZ=0
    g39: LineSegment [constr] StartX=-14.8 StartY=0 StartZ=0 EndX=-14.8 EndY=-10.5 EndZ=0
    g40: LineSegment [constr] StartX=-5 StartY=0 StartZ=0 EndX=-14.8 EndY=0 EndZ=0
    g41: LineSegment [constr] StartX=-5 StartY=-4 StartZ=0 EndX=-5 EndY=0 EndZ=0
    g42: LineSegment [constr] StartX=5 StartY=-4 StartZ=0 EndX=-5 EndY=-4 EndZ=0
    g43: LineSegment [constr] StartX=5 StartY=0 StartZ=0 EndX=5 EndY=-4 EndZ=0
    g44: LineSegment [constr] StartX=9.9 StartY=0 StartZ=0 EndX=5 EndY=0 EndZ=0
    g45: LineSegment [constr] StartX=9.9 StartY=1.3 StartZ=0 EndX=9.9 EndY=0 EndZ=0
    g46: LineSegment [constr] StartX=23.7 StartY=1.3 StartZ=0 EndX=9.9 EndY=1.3 EndZ=0
    g47: ArcOfCircle [constr] CenterX=25.2 CenterY=1.3 CenterZ=0 NormalX=-1e-16 NormalY=0 NormalZ=1 AngleXU=1.5708 Radius=1.5 StartAngle=0 EndAngle=1.5708
    g48: LineSegment [constr] StartX=43.8874 StartY=2.8 StartZ=0 EndX=25.2 EndY=2.8 EndZ=0
    g49: Circle [constr] CenterX=112.6 CenterY=-57.3 CenterZ=0 NormalX=-1e-16 NormalY=0 NormalZ=1 AngleXU=-1.5708 Radius=1.1
    g50: ArcOfCircle [constr] CenterX=60.7 CenterY=-66.9 CenterZ=0 NormalX=-1e-16 NormalY=0 NormalZ=1 AngleXU=-3.14159 Radius=1.5 StartAngle=0 EndAngle=1.5708
    g51: LineSegment [constr] StartX=59.2 StartY=-66.1 StartZ=0 EndX=59.2 EndY=-66.9 EndZ=0
    g52: LineSegment [constr] StartX=51.15 StartY=-66.1 StartZ=0 EndX=59.2 EndY=-66.1 EndZ=0
    g53: LineSegment [constr] StartX=51.15 StartY=-67.6 StartZ=0 EndX=51.15 EndY=-66.1 EndZ=0
    g54: LineSegment [constr] StartX=56.7 StartY=-67.6 StartZ=0 EndX=51.15 EndY=-67.6 EndZ=0
    g55: LineSegment [constr] StartX=56.7 StartY=-69.9 StartZ=0 EndX=56.7 EndY=-67.6 EndZ=0
    g56: LineSegment [constr] StartX=67.1 StartY=-69.9 StartZ=0 EndX=56.7 EndY=-69.9 EndZ=0
    g57: LineSegment [constr] StartX=67.1 StartY=-68.4 StartZ=0 EndX=67.1 EndY=-69.9 EndZ=0
    g58: LineSegment [constr] StartX=60.7 StartY=-68.4 StartZ=0 EndX=67.1 EndY=-68.4 EndZ=0
    g59: LineSegment [constr] StartX=62.7 StartY=-60 StartZ=0 EndX=27.8 EndY=-60 EndZ=0
    g60: LineSegment [constr] StartX=62.7 StartY=-57.6 StartZ=0 EndX=62.7 EndY=-60 EndZ=0
    g61: LineSegment [constr] StartX=27.8 StartY=-57.6 StartZ=0 EndX=62.7 EndY=-57.6 EndZ=0
    g62: LineSegment [constr] StartX=27.8 StartY=-60 StartZ=0 EndX=27.8 EndY=-57.6 EndZ=0
    g63: Circle [constr] CenterX=-14 CenterY=-73.8 CenterZ=0 NormalX=-1e-16 NormalY=0 NormalZ=1 AngleXU=-1.5708 Radius=1.1
    g64: LineSegment [constr] StartX=-14.8 StartY=-64.1 StartZ=0 EndX=-16.4 EndY=-64.1 EndZ=0
    g65: LineSegment [constr] StartX=-14.8 StartY=-54 StartZ=0 EndX=-14.8 EndY=-64.1 EndZ=0
    g66: LineSegment [constr] StartX=-16.4 StartY=-54 StartZ=0 EndX=-14.8 EndY=-54 EndZ=0
    g67: LineSegment [constr] StartX=-16.4 StartY=-64.1 StartZ=0 EndX=-16.4 EndY=-54 EndZ=0
    g68: LineSegment [constr] StartX=52 StartY=-56.2 StartZ=0 EndX=27.8 EndY=-56.2 EndZ=0
    g69: LineSegment [constr] StartX=52 StartY=-53.8 StartZ=0 EndX=52 EndY=-56.2 EndZ=0
    g70: LineSegment [constr] StartX=27.8 StartY=-53.8 StartZ=0 EndX=52 EndY=-53.8 EndZ=0
    g71: LineSegment [constr] StartX=27.8 StartY=-56.2 StartZ=0 EndX=27.8 EndY=-53.8 EndZ=0
    g72: Circle [constr] CenterX=112.6 CenterY=-23.3 CenterZ=0 NormalX=-1e-16 NormalY=0 NormalZ=1 AngleXU=-1.5708 Radius=1.1
    g73: Circle [constr] CenterX=25.9 CenterY=0.6 CenterZ=0 NormalX=-1e-16 NormalY=0 NormalZ=1 AngleXU=-1.5708 Radius=1.1
    g74: Circle [constr] CenterX=25.9 CenterY=0.6 CenterZ=0 NormalX=0 NormalY=0 NormalZ=1 AngleXU=0 Radius=1.2
    g75: Circle [constr] CenterX=25.9 CenterY=0.6 CenterZ=0 NormalX=0 NormalY=0 NormalZ=1 AngleXU=0 Radius=1.2
    g76: Circle [constr] CenterX=112.6 CenterY=-23.3 CenterZ=0 NormalX=0 NormalY=0 NormalZ=1 AngleXU=0 Radius=1.1
    g77: Circle [constr] CenterX=112.6 CenterY=-57.3 CenterZ=0 NormalX=0 NormalY=0 NormalZ=1 AngleXU=0 Radius=1.1
    g78: Circle [constr] CenterX=-14 CenterY=-73.8 CenterZ=0 NormalX=0 NormalY=0 NormalZ=1 AngleXU=0 Radius=1.2
    g79: Circle CenterX=112.6 CenterY=-23.3 CenterZ=0 NormalX=0 NormalY=0 NormalZ=1 AngleXU=0 Radius=2.5
    g80: Circle CenterX=112.6 CenterY=-57.3 CenterZ=0 NormalX=0 NormalY=0 NormalZ=1 AngleXU=0 Radius=2.5
    g81: Circle CenterX=-14 CenterY=-73.8 CenterZ=0 NormalX=0 NormalY=0 NormalZ=1 AngleXU=0 Radius=2.5
    g82: Circle CenterX=25.9 CenterY=0.6 CenterZ=0 NormalX=0 NormalY=0 NormalZ=1 AngleXU=0 Radius=2.5
  constraints (163):
    c: Coincident(g34,g35)
    c: Coincident(g35,g36)
    c: Coincident(g64,g67)
    c: Coincident(g66,g67)
    c: Coincident(g37,g38)
    c: Coincident(g36,g37)
    c: Coincident(g64,g65)
    c: Coincident(g65,g66)
    c: Coincident(g38,g39)
    c: Coincident(g39,g40)
    c: Coincident(g33,g34)
    c: Coincident(g32,g33)
    c: Coincident(g41,g42)
    c: Coincident(g40,g41)
    c: Coincident(g42,g43)
    c: Coincident(g43,g44)
    c: Coincident(g31,g32)
    c: Coincident(g44,g45)
    c: Coincident(g45,g46)
    c: Coincident(g46,g47)
    c: Coincident(g30,g31)
    c: Coincident(g47,g48)
    c: Coincident(g59,g62)
    c: Coincident(g61,g62)
    c: Coincident(g68,g71)
    c: Coincident(g70,g71)
    c: Coincident(g29,g30)
    c: Coincident(g28,g29)
    c: Coincident(g27,g28)
    c: Coincident(g26,g27)
    c: Coincident(g2,g48)
    c: Coincident(g0,g2)
    c: Coincident(g22,g23)
    c: Coincident(g23,g24)
    c: Coincident(g0,g1)
    c: Coincident(g21,g22)
    c: Coincident(g24,g25)
    c: Coincident(g25,g26)
    c: Coincident(g53,g54)
    c: Coincident(g52,g53)
    c: Coincident(g68,g69)
    c: Coincident(g69,g70)
    c: Coincident(g55,g56)
    c: Coincident(g54,g55)
    c: Coincident(g50,g51)
    c: Coincident(g51,g52)
    c: Coincident(g1,g3)
    c: Coincident(g50,g58)
    c: Coincident(g4,g5)
    c: Coincident(g3,g4)
    c: Coincident(g59,g60)
    c: Coincident(g60,g61)
    c: Coincident(g56,g57)
    c: Coincident(g57,g58)
    c: Coincident(g17,g18)
    c: Coincident(g16,g17)
    c: Coincident(g20,g21)
    c: Coincident(g19,g20)
    c: Coincident(g18,g19)
    c: Coincident(g5,g6)
    c: Coincident(g14,g15)
    c: Coincident(g15,g16)
    c: Coincident(g7,g8)
    c: Coincident(g6,g7)
    c: Coincident(g13,g14)
    c: Coincident(g12,g13)
    c: Coincident(g8,g9)
    c: Coincident(g11,g12)
    c: Coincident(g10,g11)
    c: Coincident(g9,g10)
    c: Block(g0)
    c: Block(g1)
    c: Block(g2)
    c: Block(g3)
    c: Block(g4)
    c: Block(g5)
    c: Block(g6)
    c: Block(g7)
    c: Block(g8)
    c: Block(g9)
    c: Block(g10)
    c: Block(g11)
    c: Block(g12)
    c: Block(g13)
    c: Block(g14)
    c: Block(g15)
    c: Block(g16)
    c: Block(g17)
    c: Block(g18)
    c: Block(g19)
    c: Block(g20)
    c: Block(g21)
    c: Block(g22)
    c: Block(g23)
    c: Block(g24)
    c: Block(g25)
    c: Block(g26)
    c: Block(g27)
    c: Block(g28)
    c: Block(g29)
    c: Block(g30)
    c: Block(g31)
    c: Block(g32)
    c: Block(g33)
    c: Block(g34)
    c: Block(g35)
    c: Block(g36)
    c: Block(g37)
    c: Block(g38)
    c: Block(g39)
    c: Block(g40)
    c: Block(g41)
    c: Block(g42)
    c: Block(g43)
    c: Block(g44)
    c: Block(g45)
    c: Block(g46)
    c: Block(g47)
    c: Block(g48)
    c: Block(g50)
    c: Block(g51)
    c: Block(g52)
    c: Block(g53)
    c: Block(g54)
    c: Block(g55)
    c: Block(g56)
    c: Block(g57)
    c: Block(g58)
    c: Block(g59)
    c: Block(g60)
    c: Block(g61)
    c: Block(g62)
    c: Block(g63)
    c: Block(g64)
    c: Block(g65)
    c: Block(g66)
    c: Block(g67)
    c: Block(g68)
    c: Block(g69)
    c: Block(g70)
    c: Block(g71)
    c: Block(g73)
    c: Diameter(g75) = 2.4
    c: Coincident(g75,g74)
    c: Equal(g75,g74)
    c: Coincident(g76,g72)
    c: Equal(g76,g72)
    c: Coincident(g77,g49)
    c: Equal(g77,g49)
    c: Diameter(g78) = 2.4
    c: Coincident(g78,g63)
    c: Diameter(g79) = 5
    c: Coincident(g79,g72)
    c: Diameter(g80) = 5
    c: Coincident(g80,g49)
    c: Diameter(g81) = 5
    c: Coincident(g81,g63)
    c: Diameter(g82) = 5
    c: Coincident(g82,g73)
    c: DistanceX(g-1,g72) = 112.6
    c: DistanceY(g72,g-1) = 23.3
    c: DistanceY(g49,g-1) = 57.3
    c: DistanceX(g-1,g49) = 112.6
FEATURE [PartDesign::Pocket] Pocket012
  BaseFeature = -> Fillet002
  Direction = (0,0,-1)
  Length = 5
  Length2 = 5
  Profile = -> Sketch027
  ReferenceAxis = -> Sketch027 [N_Axis]
  Refine = true
  SideType = 0
  Suppressed = false
  Type = 0
  Type2 = 0
FEATURE [Sketcher::SketchObject] Sketch037
  ArcFitTolerance = 1e-06
  AttachmentOffset = pos=(0,0,-5.1) rot=(0,0,1;0rad)
  AttachmentSupport = -> [XY_Plane004]
  ExternalTypes = [0]
  FullyConstrained = true
  MakeInternals = false
  MapMode = 5
  Placement = pos=(0,0,-5.1) rot=(0,0,1;0rad)
  _ExternalGeoVersion = 0
  sketch-geometry (5):
    g0: LineSegment StartX=-7.5 StartY=-83 StartZ=0 EndX=-10.3191 EndY=-84.0261 EndZ=0
    g1: LineSegment StartX=-10.3191 StartY=-84.0261 StartZ=0 EndX=-10.9689 EndY=-82.2406 EndZ=0
    g2: LineSegment [constr] StartX=-10.9689 StartY=-82.2406 StartZ=0 EndX=-8.14984 EndY=-81.2146 EndZ=0
    g3: LineSegment StartX=-8.14984 StartY=-81.2146 StartZ=0 EndX=-7.5 EndY=-83 EndZ=0
    g4: ArcOfCircle CenterX=-9.55938 CenterY=-81.7276 CenterZ=0 NormalX=0 NormalY=0 NormalZ=1 AngleXU=0 Radius=1.5 StartAngle=0.349066 EndAngle=3.49066
  constraints (15):
    c: Coincident(g0,g1)
    c: Coincident(g1,g2)
    c: Coincident(g2,g3)
    c: Coincident(g3,g0)
    c: Perpendicular(g2,g1)
    c: Perpendicular(g3,g2)
    c: Perpendicular(g3,g0)
    c: Coincident(g4,g2)
    c: Coincident(g4,g1)
    c: PointOnObject(g4,g2)
    c: Distance(g0,g0) = 3
    c: Angle(g-1,g0) = 0.349066
    c: DistanceX(g0,g-1) = 7.5
    c: DistanceY(g0,g-1) = 83
    c: Distance(g3,g3) = 1.9
FEATURE [PartDesign::Pocket] Pocket019
  BaseFeature = -> Pocket012
  Direction = (0,0,-1)
  Length = 2.4
  Length2 = 5
  Profile = -> Sketch037
  ReferenceAxis = -> Sketch037 [N_Axis]
  Refine = true
  Reversed = true
  SideType = 1
  Suppressed = false
  Type = 0
  Type2 = 0
FEATURE [PartDesign::Fillet] Fillet009
  Base = -> Pocket019 [Edge78,Edge80]
  BaseFeature = -> Pocket019
  Radius = 1
  Refine = true
  SupportTransform = false
  Suppressed = false
  UseAllEdges = false
FEATURE [PartDesign::Fillet] Fillet003
  Base = -> Fillet009 [Face1,Face40]
  BaseFeature = -> Fillet009
  Radius = 0.299
  Refine = true
  SupportTransform = false
  Suppressed = false
  UseAllEdges = false
FEATURE [PartDesign::Body] Body001  label="case-key"
  AllowCompound = false
  Group = -> [Sketch020,Sketch022,Sketch021,Pad010,Sketch023,Pocket008,Sketch024,Pocket009,Sketch025,Pocket010,Fillet,Fillet002,Sketch027,Pocket012,Sketch037,Pocket019,Fillet009,Fillet003]
  Origin = -> Origin004
  Tip = -> Fillet003
